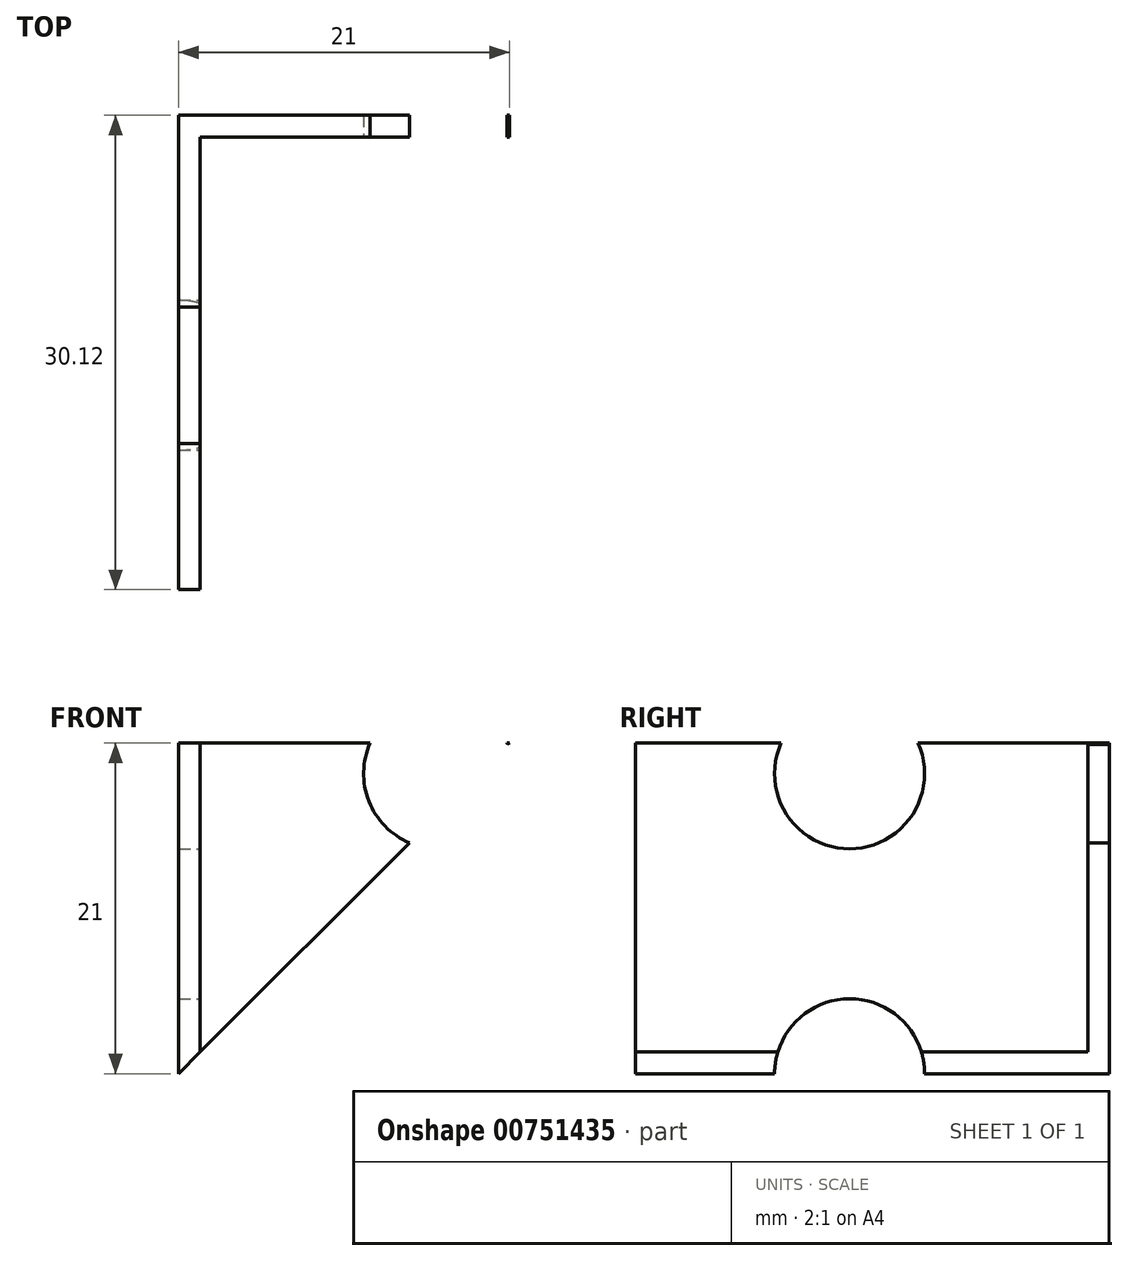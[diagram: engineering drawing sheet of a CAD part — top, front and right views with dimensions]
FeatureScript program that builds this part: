
annotation { "Feature Type Name" : "Feature", "Feature Type Description" : "" }
export const myFeature = defineFeature(function(context is Context, id is Id, definition is map)
    precondition{}
    {
        {
            assignVariable(context, id + "F0", {"name" : "height", "anyValue" : 21});
        }
        {
            var Q0;
            Q0=qCreatedBy(makeId("Top.planeOp"),FACE);
            var sketch = newSketch(context, id + "F1", { "sketchPlane" : qUnion([Q0])});
            skLineSegment(sketch, "E0", {"start": v(-1.37, -28.75) * mm, "end": v(-1.37, 1.37) * mm});
            skLineSegment(sketch, "E1", {"start": v(-1.37, 1.37) * mm, "end": v(28.75, 1.37) * mm});
            skLineSegment(sketch, "E2", {"start": v(28.75, 1.37) * mm, "end": v(28.75, 0) * mm});
            skLineSegment(sketch, "E3", {"start": v(28.75, 0) * mm, "end": v(0, 0) * mm});
            skLineSegment(sketch, "E4", {"start": v(0, 0) * mm, "end": v(0, -28.75) * mm});
            skLineSegment(sketch, "E5", {"start": v(0, -28.75) * mm, "end": v(-1.37, -28.75) * mm});
            skSolve(sketch);
        }
        {
            var Q0;
            Q0=makeQuery(id+"F1.imprint","IMPRINT",FACE,{"disambiguationData":[TD([[makeQuery(id+"F1.imprint","IMPRINT",EDGE,{"derivedFrom":sQuery(id+"F1.wireOp",EDGE,"E0")}),-1.0]])]});
            extrude(context, id + "F2", {"entities" : qUnion([Q0]), "depth" : (getVariable(context, 'height')) * mm, "offsetDistance" : 25.4 * mm});
        }
        {
            var Q0;
            Q0=makeQuery(id+"F2.opExtrude","SWEPT_FACE",FACE,{"disambiguationData":[OSD([sQuery(id+"F1.wireOp",EDGE,"E3")])]});
            var sketch = newSketch(context, id + "F3", { "sketchPlane" : qUnion([Q0])});
            skPoint(sketch, "E6", {"position": v(15.14, 19.05) * mm});
            skLineSegment(sketch, "E7", {"start": v(15.14, 0) * mm, "end": v(15.14, 533.4) * mm, "construction": true});
            skCircle(sketch, "E8", {"center": v(15.14, 19.05) * mm, "radius": 4.76 * mm});
            skCircle(sketch, "E9", {"center": v(15.14, 0) * mm, "radius": 4.76 * mm});
            skPoint(sketch, "E10", {"position": v(15.14, 38.1) * mm});
            skPoint(sketch, "E11", {"position": v(15.14, 57.15) * mm});
            skArc(sketch, "E12", {"start": v(19.9, 39.69) * mm, "mid": v(15.14, 44.45) * mm, "end": v(10.38, 39.69) * mm});
            skArc(sketch, "E13", {"start": v(10.38, 36.51) * mm, "mid": v(15.14, 31.75) * mm, "end": v(19.9, 36.51) * mm});
            skLineSegment(sketch, "E14", {"start": v(19.9, 39.69) * mm, "end": v(19.9, 36.51) * mm});
            skLineSegment(sketch, "E15", {"start": v(10.38, 39.69) * mm, "end": v(10.38, 36.51) * mm});
            skArc(sketch, "E16", {"start": v(19.9, 58.74) * mm, "mid": v(15.14, 63.5) * mm, "end": v(10.38, 58.74) * mm});
            skArc(sketch, "E17", {"start": v(10.38, 55.56) * mm, "mid": v(15.14, 50.8) * mm, "end": v(19.9, 55.56) * mm});
            skLineSegment(sketch, "E18", {"start": v(19.9, 58.74) * mm, "end": v(19.9, 55.56) * mm});
            skLineSegment(sketch, "E19", {"start": v(10.38, 58.74) * mm, "end": v(10.38, 55.56) * mm});
            skPoint(sketch, "E20.0.1.0", {"position": v(15.14, 133.35) * mm});
            skArc(sketch, "E20.0.1.1", {"start": v(19.9, 134.94) * mm, "mid": v(15.14, 139.7) * mm, "end": v(10.38, 134.94) * mm});
            skPoint(sketch, "E20.0.1.2", {"position": v(15.14, 114.3) * mm});
            skPoint(sketch, "E20.0.1.3", {"position": v(15.14, 95.25) * mm});
            skArc(sketch, "E20.0.1.4", {"start": v(10.38, 131.76) * mm, "mid": v(15.14, 127) * mm, "end": v(19.9, 131.76) * mm});
            skCircle(sketch, "E20.0.1.5", {"center": v(15.14, 95.25) * mm, "radius": 4.76 * mm});
            skCircle(sketch, "E20.0.1.6", {"center": v(15.14, 76.2) * mm, "radius": 4.76 * mm});
            skArc(sketch, "E20.0.1.7", {"start": v(19.9, 115.89) * mm, "mid": v(15.14, 120.65) * mm, "end": v(10.38, 115.89) * mm});
            skArc(sketch, "E20.0.1.8", {"start": v(10.38, 112.71) * mm, "mid": v(15.14, 107.95) * mm, "end": v(19.9, 112.71) * mm});
            skPoint(sketch, "E20.0.1.9", {"position": v(15.14, 133.35) * mm});
            skPoint(sketch, "E20.0.1.10", {"position": v(15.14, 114.3) * mm});
            skLineSegment(sketch, "E20.0.1.11", {"start": v(10.38, 134.94) * mm, "end": v(10.38, 131.76) * mm});
            skLineSegment(sketch, "E20.0.1.12", {"start": v(19.9, 134.94) * mm, "end": v(19.9, 131.76) * mm});
            skLineSegment(sketch, "E20.0.1.13", {"start": v(19.9, 115.89) * mm, "end": v(19.9, 112.71) * mm});
            skLineSegment(sketch, "E20.0.1.14", {"start": v(10.38, 115.89) * mm, "end": v(10.38, 112.71) * mm});
            skPoint(sketch, "E20.0.2.0", {"position": v(15.14, 209.55) * mm});
            skArc(sketch, "E20.0.2.1", {"start": v(19.9, 211.14) * mm, "mid": v(15.14, 215.9) * mm, "end": v(10.38, 211.14) * mm});
            skPoint(sketch, "E20.0.2.2", {"position": v(15.14, 190.5) * mm});
            skPoint(sketch, "E20.0.2.3", {"position": v(15.14, 171.45) * mm});
            skArc(sketch, "E20.0.2.4", {"start": v(10.38, 207.96) * mm, "mid": v(15.14, 203.2) * mm, "end": v(19.9, 207.96) * mm});
            skCircle(sketch, "E20.0.2.5", {"center": v(15.14, 171.45) * mm, "radius": 4.76 * mm});
            skCircle(sketch, "E20.0.2.6", {"center": v(15.14, 152.4) * mm, "radius": 4.76 * mm});
            skArc(sketch, "E20.0.2.7", {"start": v(19.9, 192.09) * mm, "mid": v(15.14, 196.85) * mm, "end": v(10.38, 192.09) * mm});
            skArc(sketch, "E20.0.2.8", {"start": v(10.38, 188.91) * mm, "mid": v(15.14, 184.15) * mm, "end": v(19.9, 188.91) * mm});
            skPoint(sketch, "E20.0.2.9", {"position": v(15.14, 209.55) * mm});
            skPoint(sketch, "E20.0.2.10", {"position": v(15.14, 190.5) * mm});
            skLineSegment(sketch, "E20.0.2.11", {"start": v(10.38, 211.14) * mm, "end": v(10.38, 207.96) * mm});
            skLineSegment(sketch, "E20.0.2.12", {"start": v(19.9, 211.14) * mm, "end": v(19.9, 207.96) * mm});
            skLineSegment(sketch, "E20.0.2.13", {"start": v(19.9, 192.09) * mm, "end": v(19.9, 188.91) * mm});
            skLineSegment(sketch, "E20.0.2.14", {"start": v(10.38, 192.09) * mm, "end": v(10.38, 188.91) * mm});
            skPoint(sketch, "E20.0.3.0", {"position": v(15.14, 285.75) * mm});
            skArc(sketch, "E20.0.3.1", {"start": v(19.9, 287.34) * mm, "mid": v(15.14, 292.1) * mm, "end": v(10.38, 287.34) * mm});
            skPoint(sketch, "E20.0.3.2", {"position": v(15.14, 266.7) * mm});
            skPoint(sketch, "E20.0.3.3", {"position": v(15.14, 247.65) * mm});
            skArc(sketch, "E20.0.3.4", {"start": v(10.38, 284.16) * mm, "mid": v(15.14, 279.4) * mm, "end": v(19.9, 284.16) * mm});
            skCircle(sketch, "E20.0.3.5", {"center": v(15.14, 247.65) * mm, "radius": 4.76 * mm});
            skCircle(sketch, "E20.0.3.6", {"center": v(15.14, 228.6) * mm, "radius": 4.76 * mm});
            skArc(sketch, "E20.0.3.7", {"start": v(19.9, 268.29) * mm, "mid": v(15.14, 273.05) * mm, "end": v(10.38, 268.29) * mm});
            skArc(sketch, "E20.0.3.8", {"start": v(10.38, 265.11) * mm, "mid": v(15.14, 260.35) * mm, "end": v(19.9, 265.11) * mm});
            skPoint(sketch, "E20.0.3.9", {"position": v(15.14, 285.75) * mm});
            skPoint(sketch, "E20.0.3.10", {"position": v(15.14, 266.7) * mm});
            skLineSegment(sketch, "E20.0.3.11", {"start": v(10.38, 287.34) * mm, "end": v(10.38, 284.16) * mm});
            skLineSegment(sketch, "E20.0.3.12", {"start": v(19.9, 287.34) * mm, "end": v(19.9, 284.16) * mm});
            skLineSegment(sketch, "E20.0.3.13", {"start": v(19.9, 268.29) * mm, "end": v(19.9, 265.11) * mm});
            skLineSegment(sketch, "E20.0.3.14", {"start": v(10.38, 268.29) * mm, "end": v(10.38, 265.11) * mm});
            skPoint(sketch, "E20.0.4.0", {"position": v(15.14, 361.95) * mm});
            skArc(sketch, "E20.0.4.1", {"start": v(19.9, 363.54) * mm, "mid": v(15.14, 368.3) * mm, "end": v(10.38, 363.54) * mm});
            skPoint(sketch, "E20.0.4.2", {"position": v(15.14, 342.9) * mm});
            skPoint(sketch, "E20.0.4.3", {"position": v(15.14, 323.85) * mm});
            skArc(sketch, "E20.0.4.4", {"start": v(10.38, 360.36) * mm, "mid": v(15.14, 355.6) * mm, "end": v(19.9, 360.36) * mm});
            skCircle(sketch, "E20.0.4.5", {"center": v(15.14, 323.85) * mm, "radius": 4.76 * mm});
            skCircle(sketch, "E20.0.4.6", {"center": v(15.14, 304.8) * mm, "radius": 4.76 * mm});
            skArc(sketch, "E20.0.4.7", {"start": v(19.9, 344.49) * mm, "mid": v(15.14, 349.25) * mm, "end": v(10.38, 344.49) * mm});
            skArc(sketch, "E20.0.4.8", {"start": v(10.38, 341.31) * mm, "mid": v(15.14, 336.55) * mm, "end": v(19.9, 341.31) * mm});
            skPoint(sketch, "E20.0.4.9", {"position": v(15.14, 361.95) * mm});
            skPoint(sketch, "E20.0.4.10", {"position": v(15.14, 342.9) * mm});
            skLineSegment(sketch, "E20.0.4.11", {"start": v(10.38, 363.54) * mm, "end": v(10.38, 360.36) * mm});
            skLineSegment(sketch, "E20.0.4.12", {"start": v(19.9, 363.54) * mm, "end": v(19.9, 360.36) * mm});
            skLineSegment(sketch, "E20.0.4.13", {"start": v(19.9, 344.49) * mm, "end": v(19.9, 341.31) * mm});
            skLineSegment(sketch, "E20.0.4.14", {"start": v(10.38, 344.49) * mm, "end": v(10.38, 341.31) * mm});
            skPoint(sketch, "E20.0.5.0", {"position": v(15.14, 438.15) * mm});
            skArc(sketch, "E20.0.5.1", {"start": v(19.9, 439.74) * mm, "mid": v(15.14, 444.5) * mm, "end": v(10.38, 439.74) * mm});
            skPoint(sketch, "E20.0.5.2", {"position": v(15.14, 419.1) * mm});
            skPoint(sketch, "E20.0.5.3", {"position": v(15.14, 400.05) * mm});
            skArc(sketch, "E20.0.5.4", {"start": v(10.38, 436.56) * mm, "mid": v(15.14, 431.8) * mm, "end": v(19.9, 436.56) * mm});
            skCircle(sketch, "E20.0.5.5", {"center": v(15.14, 400.05) * mm, "radius": 4.76 * mm});
            skCircle(sketch, "E20.0.5.6", {"center": v(15.14, 381) * mm, "radius": 4.76 * mm});
            skArc(sketch, "E20.0.5.7", {"start": v(19.9, 420.69) * mm, "mid": v(15.14, 425.45) * mm, "end": v(10.38, 420.69) * mm});
            skArc(sketch, "E20.0.5.8", {"start": v(10.38, 417.51) * mm, "mid": v(15.14, 412.75) * mm, "end": v(19.9, 417.51) * mm});
            skPoint(sketch, "E20.0.5.9", {"position": v(15.14, 438.15) * mm});
            skPoint(sketch, "E20.0.5.10", {"position": v(15.14, 419.1) * mm});
            skLineSegment(sketch, "E20.0.5.11", {"start": v(10.38, 439.74) * mm, "end": v(10.38, 436.56) * mm});
            skLineSegment(sketch, "E20.0.5.12", {"start": v(19.9, 439.74) * mm, "end": v(19.9, 436.56) * mm});
            skLineSegment(sketch, "E20.0.5.13", {"start": v(19.9, 420.69) * mm, "end": v(19.9, 417.51) * mm});
            skLineSegment(sketch, "E20.0.5.14", {"start": v(10.38, 420.69) * mm, "end": v(10.38, 417.51) * mm});
            skPoint(sketch, "E20.0.6.0", {"position": v(15.14, 514.35) * mm});
            skArc(sketch, "E20.0.6.1", {"start": v(19.9, 515.94) * mm, "mid": v(15.14, 520.7) * mm, "end": v(10.38, 515.94) * mm});
            skPoint(sketch, "E20.0.6.2", {"position": v(15.14, 495.3) * mm});
            skPoint(sketch, "E20.0.6.3", {"position": v(15.14, 476.25) * mm});
            skArc(sketch, "E20.0.6.4", {"start": v(10.38, 512.76) * mm, "mid": v(15.14, 508) * mm, "end": v(19.9, 512.76) * mm});
            skCircle(sketch, "E20.0.6.5", {"center": v(15.14, 476.25) * mm, "radius": 4.76 * mm});
            skCircle(sketch, "E20.0.6.6", {"center": v(15.14, 457.2) * mm, "radius": 4.76 * mm});
            skArc(sketch, "E20.0.6.7", {"start": v(19.9, 496.89) * mm, "mid": v(15.14, 501.65) * mm, "end": v(10.38, 496.89) * mm});
            skArc(sketch, "E20.0.6.8", {"start": v(10.38, 493.71) * mm, "mid": v(15.14, 488.95) * mm, "end": v(19.9, 493.71) * mm});
            skPoint(sketch, "E20.0.6.9", {"position": v(15.14, 514.35) * mm});
            skPoint(sketch, "E20.0.6.10", {"position": v(15.14, 495.3) * mm});
            skLineSegment(sketch, "E20.0.6.11", {"start": v(10.38, 515.94) * mm, "end": v(10.38, 512.76) * mm});
            skLineSegment(sketch, "E20.0.6.12", {"start": v(19.9, 515.94) * mm, "end": v(19.9, 512.76) * mm});
            skLineSegment(sketch, "E20.0.6.13", {"start": v(19.9, 496.89) * mm, "end": v(19.9, 493.71) * mm});
            skLineSegment(sketch, "E20.0.6.14", {"start": v(10.38, 496.89) * mm, "end": v(10.38, 493.71) * mm});
            skPoint(sketch, "E20.0.7.0", {"position": v(15.14, 590.55) * mm});
            skArc(sketch, "E20.0.7.1", {"start": v(19.9, 592.14) * mm, "mid": v(15.14, 596.9) * mm, "end": v(10.38, 592.14) * mm});
            skPoint(sketch, "E20.0.7.2", {"position": v(15.14, 571.5) * mm});
            skPoint(sketch, "E20.0.7.3", {"position": v(15.14, 552.45) * mm});
            skArc(sketch, "E20.0.7.4", {"start": v(10.38, 588.96) * mm, "mid": v(15.14, 584.2) * mm, "end": v(19.9, 588.96) * mm});
            skCircle(sketch, "E20.0.7.5", {"center": v(15.14, 552.45) * mm, "radius": 4.76 * mm});
            skCircle(sketch, "E20.0.7.6", {"center": v(15.14, 533.4) * mm, "radius": 4.76 * mm});
            skArc(sketch, "E20.0.7.7", {"start": v(19.9, 573.09) * mm, "mid": v(15.14, 577.85) * mm, "end": v(10.38, 573.09) * mm});
            skArc(sketch, "E20.0.7.8", {"start": v(10.38, 569.91) * mm, "mid": v(15.14, 565.15) * mm, "end": v(19.9, 569.91) * mm});
            skPoint(sketch, "E20.0.7.9", {"position": v(15.14, 590.55) * mm});
            skPoint(sketch, "E20.0.7.10", {"position": v(15.14, 571.5) * mm});
            skLineSegment(sketch, "E20.0.7.11", {"start": v(10.38, 592.14) * mm, "end": v(10.38, 588.96) * mm});
            skLineSegment(sketch, "E20.0.7.12", {"start": v(19.9, 592.14) * mm, "end": v(19.9, 588.96) * mm});
            skLineSegment(sketch, "E20.0.7.13", {"start": v(19.9, 573.09) * mm, "end": v(19.9, 569.91) * mm});
            skLineSegment(sketch, "E20.0.7.14", {"start": v(10.38, 573.09) * mm, "end": v(10.38, 569.91) * mm});
            skPoint(sketch, "E20.0.8.0", {"position": v(15.14, 666.75) * mm});
            skArc(sketch, "E20.0.8.1", {"start": v(19.9, 668.34) * mm, "mid": v(15.14, 673.1) * mm, "end": v(10.38, 668.34) * mm});
            skPoint(sketch, "E20.0.8.2", {"position": v(15.14, 647.7) * mm});
            skPoint(sketch, "E20.0.8.3", {"position": v(15.14, 628.65) * mm});
            skArc(sketch, "E20.0.8.4", {"start": v(10.38, 665.16) * mm, "mid": v(15.14, 660.4) * mm, "end": v(19.9, 665.16) * mm});
            skCircle(sketch, "E20.0.8.5", {"center": v(15.14, 628.65) * mm, "radius": 4.76 * mm});
            skCircle(sketch, "E20.0.8.6", {"center": v(15.14, 609.6) * mm, "radius": 4.76 * mm});
            skArc(sketch, "E20.0.8.7", {"start": v(19.9, 649.29) * mm, "mid": v(15.14, 654.05) * mm, "end": v(10.38, 649.29) * mm});
            skArc(sketch, "E20.0.8.8", {"start": v(10.38, 646.11) * mm, "mid": v(15.14, 641.35) * mm, "end": v(19.9, 646.11) * mm});
            skPoint(sketch, "E20.0.8.9", {"position": v(15.14, 666.75) * mm});
            skPoint(sketch, "E20.0.8.10", {"position": v(15.14, 647.7) * mm});
            skLineSegment(sketch, "E20.0.8.11", {"start": v(10.38, 668.34) * mm, "end": v(10.38, 665.16) * mm});
            skLineSegment(sketch, "E20.0.8.12", {"start": v(19.9, 668.34) * mm, "end": v(19.9, 665.16) * mm});
            skLineSegment(sketch, "E20.0.8.13", {"start": v(19.9, 649.29) * mm, "end": v(19.9, 646.11) * mm});
            skLineSegment(sketch, "E20.0.8.14", {"start": v(10.38, 649.29) * mm, "end": v(10.38, 646.11) * mm});
            skPoint(sketch, "E20.0.9.0", {"position": v(15.14, 742.95) * mm});
            skArc(sketch, "E20.0.9.1", {"start": v(19.9, 744.54) * mm, "mid": v(15.14, 749.3) * mm, "end": v(10.38, 744.54) * mm});
            skPoint(sketch, "E20.0.9.2", {"position": v(15.14, 723.9) * mm});
            skPoint(sketch, "E20.0.9.3", {"position": v(15.14, 704.85) * mm});
            skArc(sketch, "E20.0.9.4", {"start": v(10.38, 741.36) * mm, "mid": v(15.14, 736.6) * mm, "end": v(19.9, 741.36) * mm});
            skCircle(sketch, "E20.0.9.5", {"center": v(15.14, 704.85) * mm, "radius": 4.76 * mm});
            skCircle(sketch, "E20.0.9.6", {"center": v(15.14, 685.8) * mm, "radius": 4.76 * mm});
            skArc(sketch, "E20.0.9.7", {"start": v(19.9, 725.49) * mm, "mid": v(15.14, 730.25) * mm, "end": v(10.38, 725.49) * mm});
            skArc(sketch, "E20.0.9.8", {"start": v(10.38, 722.31) * mm, "mid": v(15.14, 717.55) * mm, "end": v(19.9, 722.31) * mm});
            skPoint(sketch, "E20.0.9.9", {"position": v(15.14, 742.95) * mm});
            skPoint(sketch, "E20.0.9.10", {"position": v(15.14, 723.9) * mm});
            skLineSegment(sketch, "E20.0.9.11", {"start": v(10.38, 744.54) * mm, "end": v(10.38, 741.36) * mm});
            skLineSegment(sketch, "E20.0.9.12", {"start": v(19.9, 744.54) * mm, "end": v(19.9, 741.36) * mm});
            skLineSegment(sketch, "E20.0.9.13", {"start": v(19.9, 725.49) * mm, "end": v(19.9, 722.31) * mm});
            skLineSegment(sketch, "E20.0.9.14", {"start": v(10.38, 725.49) * mm, "end": v(10.38, 722.31) * mm});
            skPoint(sketch, "E20.0.10.0", {"position": v(15.14, 819.15) * mm});
            skArc(sketch, "E20.0.10.1", {"start": v(19.9, 820.74) * mm, "mid": v(15.14, 825.5) * mm, "end": v(10.38, 820.74) * mm});
            skPoint(sketch, "E20.0.10.2", {"position": v(15.14, 800.1) * mm});
            skPoint(sketch, "E20.0.10.3", {"position": v(15.14, 781.05) * mm});
            skArc(sketch, "E20.0.10.4", {"start": v(10.38, 817.56) * mm, "mid": v(15.14, 812.8) * mm, "end": v(19.9, 817.56) * mm});
            skCircle(sketch, "E20.0.10.5", {"center": v(15.14, 781.05) * mm, "radius": 4.76 * mm});
            skCircle(sketch, "E20.0.10.6", {"center": v(15.14, 762) * mm, "radius": 4.76 * mm});
            skArc(sketch, "E20.0.10.7", {"start": v(19.9, 801.69) * mm, "mid": v(15.14, 806.45) * mm, "end": v(10.38, 801.69) * mm});
            skArc(sketch, "E20.0.10.8", {"start": v(10.38, 798.51) * mm, "mid": v(15.14, 793.75) * mm, "end": v(19.9, 798.51) * mm});
            skPoint(sketch, "E20.0.10.9", {"position": v(15.14, 819.15) * mm});
            skPoint(sketch, "E20.0.10.10", {"position": v(15.14, 800.1) * mm});
            skLineSegment(sketch, "E20.0.10.11", {"start": v(10.38, 820.74) * mm, "end": v(10.38, 817.56) * mm});
            skLineSegment(sketch, "E20.0.10.12", {"start": v(19.9, 820.74) * mm, "end": v(19.9, 817.56) * mm});
            skLineSegment(sketch, "E20.0.10.13", {"start": v(19.9, 801.69) * mm, "end": v(19.9, 798.51) * mm});
            skLineSegment(sketch, "E20.0.10.14", {"start": v(10.38, 801.69) * mm, "end": v(10.38, 798.51) * mm});
            skPoint(sketch, "E20.0.11.0", {"position": v(15.14, 895.35) * mm});
            skArc(sketch, "E20.0.11.1", {"start": v(19.9, 896.94) * mm, "mid": v(15.14, 901.7) * mm, "end": v(10.38, 896.94) * mm});
            skPoint(sketch, "E20.0.11.2", {"position": v(15.14, 876.3) * mm});
            skPoint(sketch, "E20.0.11.3", {"position": v(15.14, 857.25) * mm});
            skArc(sketch, "E20.0.11.4", {"start": v(10.38, 893.76) * mm, "mid": v(15.14, 889) * mm, "end": v(19.9, 893.76) * mm});
            skCircle(sketch, "E20.0.11.5", {"center": v(15.14, 857.25) * mm, "radius": 4.76 * mm});
            skCircle(sketch, "E20.0.11.6", {"center": v(15.14, 838.2) * mm, "radius": 4.76 * mm});
            skArc(sketch, "E20.0.11.7", {"start": v(19.9, 877.89) * mm, "mid": v(15.14, 882.65) * mm, "end": v(10.38, 877.89) * mm});
            skArc(sketch, "E20.0.11.8", {"start": v(10.38, 874.71) * mm, "mid": v(15.14, 869.95) * mm, "end": v(19.9, 874.71) * mm});
            skPoint(sketch, "E20.0.11.9", {"position": v(15.14, 895.35) * mm});
            skPoint(sketch, "E20.0.11.10", {"position": v(15.14, 876.3) * mm});
            skLineSegment(sketch, "E20.0.11.11", {"start": v(10.38, 896.94) * mm, "end": v(10.38, 893.76) * mm});
            skLineSegment(sketch, "E20.0.11.12", {"start": v(19.9, 896.94) * mm, "end": v(19.9, 893.76) * mm});
            skLineSegment(sketch, "E20.0.11.13", {"start": v(19.9, 877.89) * mm, "end": v(19.9, 874.71) * mm});
            skLineSegment(sketch, "E20.0.11.14", {"start": v(10.38, 877.89) * mm, "end": v(10.38, 874.71) * mm});
            skPoint(sketch, "E20.0.12.0", {"position": v(15.14, 971.55) * mm});
            skArc(sketch, "E20.0.12.1", {"start": v(19.9, 973.14) * mm, "mid": v(15.14, 977.9) * mm, "end": v(10.38, 973.14) * mm});
            skPoint(sketch, "E20.0.12.2", {"position": v(15.14, 952.5) * mm});
            skPoint(sketch, "E20.0.12.3", {"position": v(15.14, 933.45) * mm});
            skArc(sketch, "E20.0.12.4", {"start": v(10.38, 969.96) * mm, "mid": v(15.14, 965.2) * mm, "end": v(19.9, 969.96) * mm});
            skCircle(sketch, "E20.0.12.5", {"center": v(15.14, 933.45) * mm, "radius": 4.76 * mm});
            skCircle(sketch, "E20.0.12.6", {"center": v(15.14, 914.4) * mm, "radius": 4.76 * mm});
            skArc(sketch, "E20.0.12.7", {"start": v(19.9, 954.09) * mm, "mid": v(15.14, 958.85) * mm, "end": v(10.38, 954.09) * mm});
            skArc(sketch, "E20.0.12.8", {"start": v(10.38, 950.91) * mm, "mid": v(15.14, 946.15) * mm, "end": v(19.9, 950.91) * mm});
            skPoint(sketch, "E20.0.12.9", {"position": v(15.14, 971.55) * mm});
            skPoint(sketch, "E20.0.12.10", {"position": v(15.14, 952.5) * mm});
            skLineSegment(sketch, "E20.0.12.11", {"start": v(10.38, 973.14) * mm, "end": v(10.38, 969.96) * mm});
            skLineSegment(sketch, "E20.0.12.12", {"start": v(19.9, 973.14) * mm, "end": v(19.9, 969.96) * mm});
            skLineSegment(sketch, "E20.0.12.13", {"start": v(19.9, 954.09) * mm, "end": v(19.9, 950.91) * mm});
            skLineSegment(sketch, "E20.0.12.14", {"start": v(10.38, 954.09) * mm, "end": v(10.38, 950.91) * mm});
            skPoint(sketch, "E20.0.13.0", {"position": v(15.14, 1047.75) * mm});
            skArc(sketch, "E20.0.13.1", {"start": v(19.9, 1049.34) * mm, "mid": v(15.14, 1054.1) * mm, "end": v(10.38, 1049.34) * mm});
            skPoint(sketch, "E20.0.13.2", {"position": v(15.14, 1028.7) * mm});
            skPoint(sketch, "E20.0.13.3", {"position": v(15.14, 1009.65) * mm});
            skArc(sketch, "E20.0.13.4", {"start": v(10.38, 1046.16) * mm, "mid": v(15.14, 1041.4) * mm, "end": v(19.9, 1046.16) * mm});
            skCircle(sketch, "E20.0.13.5", {"center": v(15.14, 1009.65) * mm, "radius": 4.76 * mm});
            skCircle(sketch, "E20.0.13.6", {"center": v(15.14, 990.6) * mm, "radius": 4.76 * mm});
            skArc(sketch, "E20.0.13.7", {"start": v(19.9, 1030.29) * mm, "mid": v(15.14, 1035.05) * mm, "end": v(10.38, 1030.29) * mm});
            skArc(sketch, "E20.0.13.8", {"start": v(10.38, 1027.11) * mm, "mid": v(15.14, 1022.35) * mm, "end": v(19.9, 1027.11) * mm});
            skPoint(sketch, "E20.0.13.9", {"position": v(15.14, 1047.75) * mm});
            skPoint(sketch, "E20.0.13.10", {"position": v(15.14, 1028.7) * mm});
            skLineSegment(sketch, "E20.0.13.11", {"start": v(10.38, 1049.34) * mm, "end": v(10.38, 1046.16) * mm});
            skLineSegment(sketch, "E20.0.13.12", {"start": v(19.9, 1049.34) * mm, "end": v(19.9, 1046.16) * mm});
            skLineSegment(sketch, "E20.0.13.13", {"start": v(19.9, 1030.29) * mm, "end": v(19.9, 1027.11) * mm});
            skLineSegment(sketch, "E20.0.13.14", {"start": v(10.38, 1030.29) * mm, "end": v(10.38, 1027.11) * mm});
            skPoint(sketch, "E20.0.14.0", {"position": v(15.14, 1123.95) * mm});
            skArc(sketch, "E20.0.14.1", {"start": v(19.9, 1125.54) * mm, "mid": v(15.14, 1130.3) * mm, "end": v(10.38, 1125.54) * mm});
            skPoint(sketch, "E20.0.14.2", {"position": v(15.14, 1104.9) * mm});
            skPoint(sketch, "E20.0.14.3", {"position": v(15.14, 1085.85) * mm});
            skArc(sketch, "E20.0.14.4", {"start": v(10.38, 1122.36) * mm, "mid": v(15.14, 1117.6) * mm, "end": v(19.9, 1122.36) * mm});
            skCircle(sketch, "E20.0.14.5", {"center": v(15.14, 1085.85) * mm, "radius": 4.76 * mm});
            skCircle(sketch, "E20.0.14.6", {"center": v(15.14, 1066.8) * mm, "radius": 4.76 * mm});
            skArc(sketch, "E20.0.14.7", {"start": v(19.9, 1106.49) * mm, "mid": v(15.14, 1111.25) * mm, "end": v(10.38, 1106.49) * mm});
            skArc(sketch, "E20.0.14.8", {"start": v(10.38, 1103.31) * mm, "mid": v(15.14, 1098.55) * mm, "end": v(19.9, 1103.31) * mm});
            skPoint(sketch, "E20.0.14.9", {"position": v(15.14, 1123.95) * mm});
            skPoint(sketch, "E20.0.14.10", {"position": v(15.14, 1104.9) * mm});
            skLineSegment(sketch, "E20.0.14.11", {"start": v(10.38, 1125.54) * mm, "end": v(10.38, 1122.36) * mm});
            skLineSegment(sketch, "E20.0.14.12", {"start": v(19.9, 1125.54) * mm, "end": v(19.9, 1122.36) * mm});
            skLineSegment(sketch, "E20.0.14.13", {"start": v(19.9, 1106.49) * mm, "end": v(19.9, 1103.31) * mm});
            skLineSegment(sketch, "E20.0.14.14", {"start": v(10.38, 1106.49) * mm, "end": v(10.38, 1103.31) * mm});
            skPoint(sketch, "E20.0.15.0", {"position": v(15.14, 1200.15) * mm});
            skArc(sketch, "E20.0.15.1", {"start": v(19.9, 1201.74) * mm, "mid": v(15.14, 1206.5) * mm, "end": v(10.38, 1201.74) * mm});
            skPoint(sketch, "E20.0.15.2", {"position": v(15.14, 1181.1) * mm});
            skPoint(sketch, "E20.0.15.3", {"position": v(15.14, 1162.05) * mm});
            skArc(sketch, "E20.0.15.4", {"start": v(10.38, 1198.56) * mm, "mid": v(15.14, 1193.8) * mm, "end": v(19.9, 1198.56) * mm});
            skCircle(sketch, "E20.0.15.5", {"center": v(15.14, 1162.05) * mm, "radius": 4.76 * mm});
            skCircle(sketch, "E20.0.15.6", {"center": v(15.14, 1143) * mm, "radius": 4.76 * mm});
            skArc(sketch, "E20.0.15.7", {"start": v(19.9, 1182.69) * mm, "mid": v(15.14, 1187.45) * mm, "end": v(10.38, 1182.69) * mm});
            skArc(sketch, "E20.0.15.8", {"start": v(10.38, 1179.51) * mm, "mid": v(15.14, 1174.75) * mm, "end": v(19.9, 1179.51) * mm});
            skPoint(sketch, "E20.0.15.9", {"position": v(15.14, 1200.15) * mm});
            skPoint(sketch, "E20.0.15.10", {"position": v(15.14, 1181.1) * mm});
            skLineSegment(sketch, "E20.0.15.11", {"start": v(10.38, 1201.74) * mm, "end": v(10.38, 1198.56) * mm});
            skLineSegment(sketch, "E20.0.15.12", {"start": v(19.9, 1201.74) * mm, "end": v(19.9, 1198.56) * mm});
            skLineSegment(sketch, "E20.0.15.13", {"start": v(19.9, 1182.69) * mm, "end": v(19.9, 1179.51) * mm});
            skLineSegment(sketch, "E20.0.15.14", {"start": v(10.38, 1182.69) * mm, "end": v(10.38, 1179.51) * mm});
            skPoint(sketch, "E20.0.16.0", {"position": v(15.14, 1276.35) * mm});
            skArc(sketch, "E20.0.16.1", {"start": v(19.9, 1277.94) * mm, "mid": v(15.14, 1282.7) * mm, "end": v(10.38, 1277.94) * mm});
            skPoint(sketch, "E20.0.16.2", {"position": v(15.14, 1257.3) * mm});
            skPoint(sketch, "E20.0.16.3", {"position": v(15.14, 1238.25) * mm});
            skArc(sketch, "E20.0.16.4", {"start": v(10.38, 1274.76) * mm, "mid": v(15.14, 1270) * mm, "end": v(19.9, 1274.76) * mm});
            skCircle(sketch, "E20.0.16.5", {"center": v(15.14, 1238.25) * mm, "radius": 4.76 * mm});
            skCircle(sketch, "E20.0.16.6", {"center": v(15.14, 1219.2) * mm, "radius": 4.76 * mm});
            skArc(sketch, "E20.0.16.7", {"start": v(19.9, 1258.89) * mm, "mid": v(15.14, 1263.65) * mm, "end": v(10.38, 1258.89) * mm});
            skArc(sketch, "E20.0.16.8", {"start": v(10.38, 1255.71) * mm, "mid": v(15.14, 1250.95) * mm, "end": v(19.9, 1255.71) * mm});
            skPoint(sketch, "E20.0.16.9", {"position": v(15.14, 1276.35) * mm});
            skPoint(sketch, "E20.0.16.10", {"position": v(15.14, 1257.3) * mm});
            skLineSegment(sketch, "E20.0.16.11", {"start": v(10.38, 1277.94) * mm, "end": v(10.38, 1274.76) * mm});
            skLineSegment(sketch, "E20.0.16.12", {"start": v(19.9, 1277.94) * mm, "end": v(19.9, 1274.76) * mm});
            skLineSegment(sketch, "E20.0.16.13", {"start": v(19.9, 1258.89) * mm, "end": v(19.9, 1255.71) * mm});
            skLineSegment(sketch, "E20.0.16.14", {"start": v(10.38, 1258.89) * mm, "end": v(10.38, 1255.71) * mm});
            skPoint(sketch, "E20.0.17.0", {"position": v(15.14, 1352.55) * mm});
            skArc(sketch, "E20.0.17.1", {"start": v(19.9, 1354.14) * mm, "mid": v(15.14, 1358.9) * mm, "end": v(10.38, 1354.14) * mm});
            skPoint(sketch, "E20.0.17.2", {"position": v(15.14, 1333.5) * mm});
            skPoint(sketch, "E20.0.17.3", {"position": v(15.14, 1314.45) * mm});
            skArc(sketch, "E20.0.17.4", {"start": v(10.38, 1350.96) * mm, "mid": v(15.14, 1346.2) * mm, "end": v(19.9, 1350.96) * mm});
            skCircle(sketch, "E20.0.17.5", {"center": v(15.14, 1314.45) * mm, "radius": 4.76 * mm});
            skCircle(sketch, "E20.0.17.6", {"center": v(15.14, 1295.4) * mm, "radius": 4.76 * mm});
            skArc(sketch, "E20.0.17.7", {"start": v(19.9, 1335.09) * mm, "mid": v(15.14, 1339.85) * mm, "end": v(10.38, 1335.09) * mm});
            skArc(sketch, "E20.0.17.8", {"start": v(10.38, 1331.91) * mm, "mid": v(15.14, 1327.15) * mm, "end": v(19.9, 1331.91) * mm});
            skPoint(sketch, "E20.0.17.9", {"position": v(15.14, 1352.55) * mm});
            skPoint(sketch, "E20.0.17.10", {"position": v(15.14, 1333.5) * mm});
            skLineSegment(sketch, "E20.0.17.11", {"start": v(10.38, 1354.14) * mm, "end": v(10.38, 1350.96) * mm});
            skLineSegment(sketch, "E20.0.17.12", {"start": v(19.9, 1354.14) * mm, "end": v(19.9, 1350.96) * mm});
            skLineSegment(sketch, "E20.0.17.13", {"start": v(19.9, 1335.09) * mm, "end": v(19.9, 1331.91) * mm});
            skLineSegment(sketch, "E20.0.17.14", {"start": v(10.38, 1335.09) * mm, "end": v(10.38, 1331.91) * mm});
            skPoint(sketch, "E20.0.18.0", {"position": v(15.14, 1428.75) * mm});
            skArc(sketch, "E20.0.18.1", {"start": v(19.9, 1430.34) * mm, "mid": v(15.14, 1435.1) * mm, "end": v(10.38, 1430.34) * mm});
            skPoint(sketch, "E20.0.18.2", {"position": v(15.14, 1409.7) * mm});
            skPoint(sketch, "E20.0.18.3", {"position": v(15.14, 1390.65) * mm});
            skArc(sketch, "E20.0.18.4", {"start": v(10.38, 1427.16) * mm, "mid": v(15.14, 1422.4) * mm, "end": v(19.9, 1427.16) * mm});
            skCircle(sketch, "E20.0.18.5", {"center": v(15.14, 1390.65) * mm, "radius": 4.76 * mm});
            skCircle(sketch, "E20.0.18.6", {"center": v(15.14, 1371.6) * mm, "radius": 4.76 * mm});
            skArc(sketch, "E20.0.18.7", {"start": v(19.9, 1411.29) * mm, "mid": v(15.14, 1416.05) * mm, "end": v(10.38, 1411.29) * mm});
            skArc(sketch, "E20.0.18.8", {"start": v(10.38, 1408.11) * mm, "mid": v(15.14, 1403.35) * mm, "end": v(19.9, 1408.11) * mm});
            skPoint(sketch, "E20.0.18.9", {"position": v(15.14, 1428.75) * mm});
            skPoint(sketch, "E20.0.18.10", {"position": v(15.14, 1409.7) * mm});
            skLineSegment(sketch, "E20.0.18.11", {"start": v(10.38, 1430.34) * mm, "end": v(10.38, 1427.16) * mm});
            skLineSegment(sketch, "E20.0.18.12", {"start": v(19.9, 1430.34) * mm, "end": v(19.9, 1427.16) * mm});
            skLineSegment(sketch, "E20.0.18.13", {"start": v(19.9, 1411.29) * mm, "end": v(19.9, 1408.11) * mm});
            skLineSegment(sketch, "E20.0.18.14", {"start": v(10.38, 1411.29) * mm, "end": v(10.38, 1408.11) * mm});
            skPoint(sketch, "E20.0.19.0", {"position": v(15.14, 1504.95) * mm});
            skArc(sketch, "E20.0.19.1", {"start": v(19.9, 1506.54) * mm, "mid": v(15.14, 1511.3) * mm, "end": v(10.38, 1506.54) * mm});
            skPoint(sketch, "E20.0.19.2", {"position": v(15.14, 1485.9) * mm});
            skPoint(sketch, "E20.0.19.3", {"position": v(15.14, 1466.85) * mm});
            skArc(sketch, "E20.0.19.4", {"start": v(10.38, 1503.36) * mm, "mid": v(15.14, 1498.6) * mm, "end": v(19.9, 1503.36) * mm});
            skCircle(sketch, "E20.0.19.5", {"center": v(15.14, 1466.85) * mm, "radius": 4.76 * mm});
            skCircle(sketch, "E20.0.19.6", {"center": v(15.14, 1447.8) * mm, "radius": 4.76 * mm});
            skArc(sketch, "E20.0.19.7", {"start": v(19.9, 1487.49) * mm, "mid": v(15.14, 1492.25) * mm, "end": v(10.38, 1487.49) * mm});
            skArc(sketch, "E20.0.19.8", {"start": v(10.38, 1484.31) * mm, "mid": v(15.14, 1479.55) * mm, "end": v(19.9, 1484.31) * mm});
            skPoint(sketch, "E20.0.19.9", {"position": v(15.14, 1504.95) * mm});
            skPoint(sketch, "E20.0.19.10", {"position": v(15.14, 1485.9) * mm});
            skLineSegment(sketch, "E20.0.19.11", {"start": v(10.38, 1506.54) * mm, "end": v(10.38, 1503.36) * mm});
            skLineSegment(sketch, "E20.0.19.12", {"start": v(19.9, 1506.54) * mm, "end": v(19.9, 1503.36) * mm});
            skLineSegment(sketch, "E20.0.19.13", {"start": v(19.9, 1487.49) * mm, "end": v(19.9, 1484.31) * mm});
            skLineSegment(sketch, "E20.0.19.14", {"start": v(10.38, 1487.49) * mm, "end": v(10.38, 1484.31) * mm});
            skPoint(sketch, "E20.0.20.0", {"position": v(15.14, 1581.15) * mm});
            skArc(sketch, "E20.0.20.1", {"start": v(19.9, 1582.74) * mm, "mid": v(15.14, 1587.5) * mm, "end": v(10.38, 1582.74) * mm});
            skPoint(sketch, "E20.0.20.2", {"position": v(15.14, 1562.1) * mm});
            skPoint(sketch, "E20.0.20.3", {"position": v(15.14, 1543.05) * mm});
            skArc(sketch, "E20.0.20.4", {"start": v(10.38, 1579.56) * mm, "mid": v(15.14, 1574.8) * mm, "end": v(19.9, 1579.56) * mm});
            skCircle(sketch, "E20.0.20.5", {"center": v(15.14, 1543.05) * mm, "radius": 4.76 * mm});
            skCircle(sketch, "E20.0.20.6", {"center": v(15.14, 1524) * mm, "radius": 4.76 * mm});
            skArc(sketch, "E20.0.20.7", {"start": v(19.9, 1563.69) * mm, "mid": v(15.14, 1568.45) * mm, "end": v(10.38, 1563.69) * mm});
            skArc(sketch, "E20.0.20.8", {"start": v(10.38, 1560.51) * mm, "mid": v(15.14, 1555.75) * mm, "end": v(19.9, 1560.51) * mm});
            skPoint(sketch, "E20.0.20.9", {"position": v(15.14, 1581.15) * mm});
            skPoint(sketch, "E20.0.20.10", {"position": v(15.14, 1562.1) * mm});
            skLineSegment(sketch, "E20.0.20.11", {"start": v(10.38, 1582.74) * mm, "end": v(10.38, 1579.56) * mm});
            skLineSegment(sketch, "E20.0.20.12", {"start": v(19.9, 1582.74) * mm, "end": v(19.9, 1579.56) * mm});
            skLineSegment(sketch, "E20.0.20.13", {"start": v(19.9, 1563.69) * mm, "end": v(19.9, 1560.51) * mm});
            skLineSegment(sketch, "E20.0.20.14", {"start": v(10.38, 1563.69) * mm, "end": v(10.38, 1560.51) * mm});
            skPoint(sketch, "E20.0.21.0", {"position": v(15.14, 1657.35) * mm});
            skArc(sketch, "E20.0.21.1", {"start": v(19.9, 1658.94) * mm, "mid": v(15.14, 1663.7) * mm, "end": v(10.38, 1658.94) * mm});
            skPoint(sketch, "E20.0.21.2", {"position": v(15.14, 1638.3) * mm});
            skPoint(sketch, "E20.0.21.3", {"position": v(15.14, 1619.25) * mm});
            skArc(sketch, "E20.0.21.4", {"start": v(10.38, 1655.76) * mm, "mid": v(15.14, 1651) * mm, "end": v(19.9, 1655.76) * mm});
            skCircle(sketch, "E20.0.21.5", {"center": v(15.14, 1619.25) * mm, "radius": 4.76 * mm});
            skCircle(sketch, "E20.0.21.6", {"center": v(15.14, 1600.2) * mm, "radius": 4.76 * mm});
            skArc(sketch, "E20.0.21.7", {"start": v(19.9, 1639.89) * mm, "mid": v(15.14, 1644.65) * mm, "end": v(10.38, 1639.89) * mm});
            skArc(sketch, "E20.0.21.8", {"start": v(10.38, 1636.71) * mm, "mid": v(15.14, 1631.95) * mm, "end": v(19.9, 1636.71) * mm});
            skPoint(sketch, "E20.0.21.9", {"position": v(15.14, 1657.35) * mm});
            skPoint(sketch, "E20.0.21.10", {"position": v(15.14, 1638.3) * mm});
            skLineSegment(sketch, "E20.0.21.11", {"start": v(10.38, 1658.94) * mm, "end": v(10.38, 1655.76) * mm});
            skLineSegment(sketch, "E20.0.21.12", {"start": v(19.9, 1658.94) * mm, "end": v(19.9, 1655.76) * mm});
            skLineSegment(sketch, "E20.0.21.13", {"start": v(19.9, 1639.89) * mm, "end": v(19.9, 1636.71) * mm});
            skLineSegment(sketch, "E20.0.21.14", {"start": v(10.38, 1639.89) * mm, "end": v(10.38, 1636.71) * mm});
            skPoint(sketch, "E20.0.22.0", {"position": v(15.14, 1733.55) * mm});
            skArc(sketch, "E20.0.22.1", {"start": v(19.9, 1735.14) * mm, "mid": v(15.14, 1739.9) * mm, "end": v(10.38, 1735.14) * mm});
            skPoint(sketch, "E20.0.22.2", {"position": v(15.14, 1714.5) * mm});
            skPoint(sketch, "E20.0.22.3", {"position": v(15.14, 1695.45) * mm});
            skArc(sketch, "E20.0.22.4", {"start": v(10.38, 1731.96) * mm, "mid": v(15.14, 1727.2) * mm, "end": v(19.9, 1731.96) * mm});
            skCircle(sketch, "E20.0.22.5", {"center": v(15.14, 1695.45) * mm, "radius": 4.76 * mm});
            skCircle(sketch, "E20.0.22.6", {"center": v(15.14, 1676.4) * mm, "radius": 4.76 * mm});
            skArc(sketch, "E20.0.22.7", {"start": v(19.9, 1716.09) * mm, "mid": v(15.14, 1720.85) * mm, "end": v(10.38, 1716.09) * mm});
            skArc(sketch, "E20.0.22.8", {"start": v(10.38, 1712.91) * mm, "mid": v(15.14, 1708.15) * mm, "end": v(19.9, 1712.91) * mm});
            skPoint(sketch, "E20.0.22.9", {"position": v(15.14, 1733.55) * mm});
            skPoint(sketch, "E20.0.22.10", {"position": v(15.14, 1714.5) * mm});
            skLineSegment(sketch, "E20.0.22.11", {"start": v(10.38, 1735.14) * mm, "end": v(10.38, 1731.96) * mm});
            skLineSegment(sketch, "E20.0.22.12", {"start": v(19.9, 1735.14) * mm, "end": v(19.9, 1731.96) * mm});
            skLineSegment(sketch, "E20.0.22.13", {"start": v(19.9, 1716.09) * mm, "end": v(19.9, 1712.91) * mm});
            skLineSegment(sketch, "E20.0.22.14", {"start": v(10.38, 1716.09) * mm, "end": v(10.38, 1712.91) * mm});
            skPoint(sketch, "E20.0.23.0", {"position": v(15.14, 1809.75) * mm});
            skArc(sketch, "E20.0.23.1", {"start": v(19.9, 1811.34) * mm, "mid": v(15.14, 1816.1) * mm, "end": v(10.38, 1811.34) * mm});
            skPoint(sketch, "E20.0.23.2", {"position": v(15.14, 1790.7) * mm});
            skPoint(sketch, "E20.0.23.3", {"position": v(15.14, 1771.65) * mm});
            skArc(sketch, "E20.0.23.4", {"start": v(10.38, 1808.16) * mm, "mid": v(15.14, 1803.4) * mm, "end": v(19.9, 1808.16) * mm});
            skCircle(sketch, "E20.0.23.5", {"center": v(15.14, 1771.65) * mm, "radius": 4.76 * mm});
            skCircle(sketch, "E20.0.23.6", {"center": v(15.14, 1752.6) * mm, "radius": 4.76 * mm});
            skArc(sketch, "E20.0.23.7", {"start": v(19.9, 1792.29) * mm, "mid": v(15.14, 1797.05) * mm, "end": v(10.38, 1792.29) * mm});
            skArc(sketch, "E20.0.23.8", {"start": v(10.38, 1789.11) * mm, "mid": v(15.14, 1784.35) * mm, "end": v(19.9, 1789.11) * mm});
            skPoint(sketch, "E20.0.23.9", {"position": v(15.14, 1809.75) * mm});
            skPoint(sketch, "E20.0.23.10", {"position": v(15.14, 1790.7) * mm});
            skLineSegment(sketch, "E20.0.23.11", {"start": v(10.38, 1811.34) * mm, "end": v(10.38, 1808.16) * mm});
            skLineSegment(sketch, "E20.0.23.12", {"start": v(19.9, 1811.34) * mm, "end": v(19.9, 1808.16) * mm});
            skLineSegment(sketch, "E20.0.23.13", {"start": v(19.9, 1792.29) * mm, "end": v(19.9, 1789.11) * mm});
            skLineSegment(sketch, "E20.0.23.14", {"start": v(10.38, 1792.29) * mm, "end": v(10.38, 1789.11) * mm});
            skLineSegment(sketch, "E20.direction1", {"start": v(15.14, 0) * mm, "end": v(40.54, 0) * mm, "construction": true});
            skLineSegment(sketch, "E20.direction2", {"start": v(15.14, 0) * mm, "end": v(15.14, 76.2) * mm, "construction": true});
            skSolve(sketch);
        }
        {
            var Q0;
            Q0=makeQuery(id+"F2.opExtrude","SWEPT_FACE",FACE,{"disambiguationData":[OSD([sQuery(id+"F1.wireOp",EDGE,"E4")])]});
            var sketch = newSketch(context, id + "F4", { "sketchPlane" : qUnion([Q0])});
            skPoint(sketch, "E21", {"position": v(-15.14, 19.05) * mm});
            skLineSegment(sketch, "E22", {"start": v(-15.14, 0) * mm, "end": v(-15.14, 533.4) * mm, "construction": true});
            skCircle(sketch, "E23", {"center": v(-15.14, 19.05) * mm, "radius": 4.76 * mm});
            skCircle(sketch, "E24", {"center": v(-15.14, 0) * mm, "radius": 4.76 * mm});
            skPoint(sketch, "E25", {"position": v(-15.14, 38.1) * mm});
            skPoint(sketch, "E26", {"position": v(-15.14, 57.15) * mm});
            skArc(sketch, "E27", {"start": v(-10.38, 39.69) * mm, "mid": v(-15.14, 44.45) * mm, "end": v(-19.9, 39.69) * mm});
            skArc(sketch, "E28", {"start": v(-19.9, 36.51) * mm, "mid": v(-15.14, 31.75) * mm, "end": v(-10.38, 36.51) * mm});
            skLineSegment(sketch, "E29", {"start": v(-10.38, 39.69) * mm, "end": v(-10.38, 36.51) * mm});
            skLineSegment(sketch, "E30", {"start": v(-19.9, 39.69) * mm, "end": v(-19.9, 36.51) * mm});
            skArc(sketch, "E31", {"start": v(-10.38, 58.74) * mm, "mid": v(-15.14, 63.5) * mm, "end": v(-19.9, 58.74) * mm});
            skArc(sketch, "E32", {"start": v(-19.9, 55.56) * mm, "mid": v(-15.14, 50.8) * mm, "end": v(-10.38, 55.56) * mm});
            skLineSegment(sketch, "E33", {"start": v(-10.38, 58.74) * mm, "end": v(-10.38, 55.56) * mm});
            skLineSegment(sketch, "E34", {"start": v(-19.9, 58.74) * mm, "end": v(-19.9, 55.56) * mm});
            skPoint(sketch, "E35.0.1.0", {"position": v(-15.14, 133.35) * mm});
            skArc(sketch, "E35.0.1.1", {"start": v(-10.38, 134.94) * mm, "mid": v(-15.14, 139.7) * mm, "end": v(-19.9, 134.94) * mm});
            skPoint(sketch, "E35.0.1.2", {"position": v(-15.14, 114.3) * mm});
            skPoint(sketch, "E35.0.1.3", {"position": v(-15.14, 95.25) * mm});
            skArc(sketch, "E35.0.1.4", {"start": v(-19.9, 131.76) * mm, "mid": v(-15.14, 127) * mm, "end": v(-10.38, 131.76) * mm});
            skCircle(sketch, "E35.0.1.5", {"center": v(-15.14, 95.25) * mm, "radius": 4.76 * mm});
            skCircle(sketch, "E35.0.1.6", {"center": v(-15.14, 76.2) * mm, "radius": 4.76 * mm});
            skArc(sketch, "E35.0.1.7", {"start": v(-10.38, 115.89) * mm, "mid": v(-15.14, 120.65) * mm, "end": v(-19.9, 115.89) * mm});
            skArc(sketch, "E35.0.1.8", {"start": v(-19.9, 112.71) * mm, "mid": v(-15.14, 107.95) * mm, "end": v(-10.38, 112.71) * mm});
            skPoint(sketch, "E35.0.1.9", {"position": v(-15.14, 133.35) * mm});
            skPoint(sketch, "E35.0.1.10", {"position": v(-15.14, 114.3) * mm});
            skLineSegment(sketch, "E35.0.1.11", {"start": v(-19.9, 134.94) * mm, "end": v(-19.9, 131.76) * mm});
            skLineSegment(sketch, "E35.0.1.12", {"start": v(-10.38, 134.94) * mm, "end": v(-10.38, 131.76) * mm});
            skLineSegment(sketch, "E35.0.1.13", {"start": v(-10.38, 115.89) * mm, "end": v(-10.38, 112.71) * mm});
            skLineSegment(sketch, "E35.0.1.14", {"start": v(-19.9, 115.89) * mm, "end": v(-19.9, 112.71) * mm});
            skPoint(sketch, "E35.0.2.0", {"position": v(-15.14, 209.55) * mm});
            skArc(sketch, "E35.0.2.1", {"start": v(-10.38, 211.14) * mm, "mid": v(-15.14, 215.9) * mm, "end": v(-19.9, 211.14) * mm});
            skPoint(sketch, "E35.0.2.2", {"position": v(-15.14, 190.5) * mm});
            skPoint(sketch, "E35.0.2.3", {"position": v(-15.14, 171.45) * mm});
            skArc(sketch, "E35.0.2.4", {"start": v(-19.9, 207.96) * mm, "mid": v(-15.14, 203.2) * mm, "end": v(-10.38, 207.96) * mm});
            skCircle(sketch, "E35.0.2.5", {"center": v(-15.14, 171.45) * mm, "radius": 4.76 * mm});
            skCircle(sketch, "E35.0.2.6", {"center": v(-15.14, 152.4) * mm, "radius": 4.76 * mm});
            skArc(sketch, "E35.0.2.7", {"start": v(-10.38, 192.09) * mm, "mid": v(-15.14, 196.85) * mm, "end": v(-19.9, 192.09) * mm});
            skArc(sketch, "E35.0.2.8", {"start": v(-19.9, 188.91) * mm, "mid": v(-15.14, 184.15) * mm, "end": v(-10.38, 188.91) * mm});
            skPoint(sketch, "E35.0.2.9", {"position": v(-15.14, 209.55) * mm});
            skPoint(sketch, "E35.0.2.10", {"position": v(-15.14, 190.5) * mm});
            skLineSegment(sketch, "E35.0.2.11", {"start": v(-19.9, 211.14) * mm, "end": v(-19.9, 207.96) * mm});
            skLineSegment(sketch, "E35.0.2.12", {"start": v(-10.38, 211.14) * mm, "end": v(-10.38, 207.96) * mm});
            skLineSegment(sketch, "E35.0.2.13", {"start": v(-10.38, 192.09) * mm, "end": v(-10.38, 188.91) * mm});
            skLineSegment(sketch, "E35.0.2.14", {"start": v(-19.9, 192.09) * mm, "end": v(-19.9, 188.91) * mm});
            skPoint(sketch, "E35.0.3.0", {"position": v(-15.14, 285.75) * mm});
            skArc(sketch, "E35.0.3.1", {"start": v(-10.38, 287.34) * mm, "mid": v(-15.14, 292.1) * mm, "end": v(-19.9, 287.34) * mm});
            skPoint(sketch, "E35.0.3.2", {"position": v(-15.14, 266.7) * mm});
            skPoint(sketch, "E35.0.3.3", {"position": v(-15.14, 247.65) * mm});
            skArc(sketch, "E35.0.3.4", {"start": v(-19.9, 284.16) * mm, "mid": v(-15.14, 279.4) * mm, "end": v(-10.38, 284.16) * mm});
            skCircle(sketch, "E35.0.3.5", {"center": v(-15.14, 247.65) * mm, "radius": 4.76 * mm});
            skCircle(sketch, "E35.0.3.6", {"center": v(-15.14, 228.6) * mm, "radius": 4.76 * mm});
            skArc(sketch, "E35.0.3.7", {"start": v(-10.38, 268.29) * mm, "mid": v(-15.14, 273.05) * mm, "end": v(-19.9, 268.29) * mm});
            skArc(sketch, "E35.0.3.8", {"start": v(-19.9, 265.11) * mm, "mid": v(-15.14, 260.35) * mm, "end": v(-10.38, 265.11) * mm});
            skPoint(sketch, "E35.0.3.9", {"position": v(-15.14, 285.75) * mm});
            skPoint(sketch, "E35.0.3.10", {"position": v(-15.14, 266.7) * mm});
            skLineSegment(sketch, "E35.0.3.11", {"start": v(-19.9, 287.34) * mm, "end": v(-19.9, 284.16) * mm});
            skLineSegment(sketch, "E35.0.3.12", {"start": v(-10.38, 287.34) * mm, "end": v(-10.38, 284.16) * mm});
            skLineSegment(sketch, "E35.0.3.13", {"start": v(-10.38, 268.29) * mm, "end": v(-10.38, 265.11) * mm});
            skLineSegment(sketch, "E35.0.3.14", {"start": v(-19.9, 268.29) * mm, "end": v(-19.9, 265.11) * mm});
            skPoint(sketch, "E35.0.4.0", {"position": v(-15.14, 361.95) * mm});
            skArc(sketch, "E35.0.4.1", {"start": v(-10.38, 363.54) * mm, "mid": v(-15.14, 368.3) * mm, "end": v(-19.9, 363.54) * mm});
            skPoint(sketch, "E35.0.4.2", {"position": v(-15.14, 342.9) * mm});
            skPoint(sketch, "E35.0.4.3", {"position": v(-15.14, 323.85) * mm});
            skArc(sketch, "E35.0.4.4", {"start": v(-19.9, 360.36) * mm, "mid": v(-15.14, 355.6) * mm, "end": v(-10.38, 360.36) * mm});
            skCircle(sketch, "E35.0.4.5", {"center": v(-15.14, 323.85) * mm, "radius": 4.76 * mm});
            skCircle(sketch, "E35.0.4.6", {"center": v(-15.14, 304.8) * mm, "radius": 4.76 * mm});
            skArc(sketch, "E35.0.4.7", {"start": v(-10.38, 344.49) * mm, "mid": v(-15.14, 349.25) * mm, "end": v(-19.9, 344.49) * mm});
            skArc(sketch, "E35.0.4.8", {"start": v(-19.9, 341.31) * mm, "mid": v(-15.14, 336.55) * mm, "end": v(-10.38, 341.31) * mm});
            skPoint(sketch, "E35.0.4.9", {"position": v(-15.14, 361.95) * mm});
            skPoint(sketch, "E35.0.4.10", {"position": v(-15.14, 342.9) * mm});
            skLineSegment(sketch, "E35.0.4.11", {"start": v(-19.9, 363.54) * mm, "end": v(-19.9, 360.36) * mm});
            skLineSegment(sketch, "E35.0.4.12", {"start": v(-10.38, 363.54) * mm, "end": v(-10.38, 360.36) * mm});
            skLineSegment(sketch, "E35.0.4.13", {"start": v(-10.38, 344.49) * mm, "end": v(-10.38, 341.31) * mm});
            skLineSegment(sketch, "E35.0.4.14", {"start": v(-19.9, 344.49) * mm, "end": v(-19.9, 341.31) * mm});
            skPoint(sketch, "E35.0.5.0", {"position": v(-15.14, 438.15) * mm});
            skArc(sketch, "E35.0.5.1", {"start": v(-10.38, 439.74) * mm, "mid": v(-15.14, 444.5) * mm, "end": v(-19.9, 439.74) * mm});
            skPoint(sketch, "E35.0.5.2", {"position": v(-15.14, 419.1) * mm});
            skPoint(sketch, "E35.0.5.3", {"position": v(-15.14, 400.05) * mm});
            skArc(sketch, "E35.0.5.4", {"start": v(-19.9, 436.56) * mm, "mid": v(-15.14, 431.8) * mm, "end": v(-10.38, 436.56) * mm});
            skCircle(sketch, "E35.0.5.5", {"center": v(-15.14, 400.05) * mm, "radius": 4.76 * mm});
            skCircle(sketch, "E35.0.5.6", {"center": v(-15.14, 381) * mm, "radius": 4.76 * mm});
            skArc(sketch, "E35.0.5.7", {"start": v(-10.38, 420.69) * mm, "mid": v(-15.14, 425.45) * mm, "end": v(-19.9, 420.69) * mm});
            skArc(sketch, "E35.0.5.8", {"start": v(-19.9, 417.51) * mm, "mid": v(-15.14, 412.75) * mm, "end": v(-10.38, 417.51) * mm});
            skPoint(sketch, "E35.0.5.9", {"position": v(-15.14, 438.15) * mm});
            skPoint(sketch, "E35.0.5.10", {"position": v(-15.14, 419.1) * mm});
            skLineSegment(sketch, "E35.0.5.11", {"start": v(-19.9, 439.74) * mm, "end": v(-19.9, 436.56) * mm});
            skLineSegment(sketch, "E35.0.5.12", {"start": v(-10.38, 439.74) * mm, "end": v(-10.38, 436.56) * mm});
            skLineSegment(sketch, "E35.0.5.13", {"start": v(-10.38, 420.69) * mm, "end": v(-10.38, 417.51) * mm});
            skLineSegment(sketch, "E35.0.5.14", {"start": v(-19.9, 420.69) * mm, "end": v(-19.9, 417.51) * mm});
            skPoint(sketch, "E35.0.6.0", {"position": v(-15.14, 514.35) * mm});
            skArc(sketch, "E35.0.6.1", {"start": v(-10.38, 515.94) * mm, "mid": v(-15.14, 520.7) * mm, "end": v(-19.9, 515.94) * mm});
            skPoint(sketch, "E35.0.6.2", {"position": v(-15.14, 495.3) * mm});
            skPoint(sketch, "E35.0.6.3", {"position": v(-15.14, 476.25) * mm});
            skArc(sketch, "E35.0.6.4", {"start": v(-19.9, 512.76) * mm, "mid": v(-15.14, 508) * mm, "end": v(-10.38, 512.76) * mm});
            skCircle(sketch, "E35.0.6.5", {"center": v(-15.14, 476.25) * mm, "radius": 4.76 * mm});
            skCircle(sketch, "E35.0.6.6", {"center": v(-15.14, 457.2) * mm, "radius": 4.76 * mm});
            skArc(sketch, "E35.0.6.7", {"start": v(-10.38, 496.89) * mm, "mid": v(-15.14, 501.65) * mm, "end": v(-19.9, 496.89) * mm});
            skArc(sketch, "E35.0.6.8", {"start": v(-19.9, 493.71) * mm, "mid": v(-15.14, 488.95) * mm, "end": v(-10.38, 493.71) * mm});
            skPoint(sketch, "E35.0.6.9", {"position": v(-15.14, 514.35) * mm});
            skPoint(sketch, "E35.0.6.10", {"position": v(-15.14, 495.3) * mm});
            skLineSegment(sketch, "E35.0.6.11", {"start": v(-19.9, 515.94) * mm, "end": v(-19.9, 512.76) * mm});
            skLineSegment(sketch, "E35.0.6.12", {"start": v(-10.38, 515.94) * mm, "end": v(-10.38, 512.76) * mm});
            skLineSegment(sketch, "E35.0.6.13", {"start": v(-10.38, 496.89) * mm, "end": v(-10.38, 493.71) * mm});
            skLineSegment(sketch, "E35.0.6.14", {"start": v(-19.9, 496.89) * mm, "end": v(-19.9, 493.71) * mm});
            skPoint(sketch, "E35.0.7.0", {"position": v(-15.14, 590.55) * mm});
            skArc(sketch, "E35.0.7.1", {"start": v(-10.38, 592.14) * mm, "mid": v(-15.14, 596.9) * mm, "end": v(-19.9, 592.14) * mm});
            skPoint(sketch, "E35.0.7.2", {"position": v(-15.14, 571.5) * mm});
            skPoint(sketch, "E35.0.7.3", {"position": v(-15.14, 552.45) * mm});
            skArc(sketch, "E35.0.7.4", {"start": v(-19.9, 588.96) * mm, "mid": v(-15.14, 584.2) * mm, "end": v(-10.38, 588.96) * mm});
            skCircle(sketch, "E35.0.7.5", {"center": v(-15.14, 552.45) * mm, "radius": 4.76 * mm});
            skCircle(sketch, "E35.0.7.6", {"center": v(-15.14, 533.4) * mm, "radius": 4.76 * mm});
            skArc(sketch, "E35.0.7.7", {"start": v(-10.38, 573.09) * mm, "mid": v(-15.14, 577.85) * mm, "end": v(-19.9, 573.09) * mm});
            skArc(sketch, "E35.0.7.8", {"start": v(-19.9, 569.91) * mm, "mid": v(-15.14, 565.15) * mm, "end": v(-10.38, 569.91) * mm});
            skPoint(sketch, "E35.0.7.9", {"position": v(-15.14, 590.55) * mm});
            skPoint(sketch, "E35.0.7.10", {"position": v(-15.14, 571.5) * mm});
            skLineSegment(sketch, "E35.0.7.11", {"start": v(-19.9, 592.14) * mm, "end": v(-19.9, 588.96) * mm});
            skLineSegment(sketch, "E35.0.7.12", {"start": v(-10.38, 592.14) * mm, "end": v(-10.38, 588.96) * mm});
            skLineSegment(sketch, "E35.0.7.13", {"start": v(-10.38, 573.09) * mm, "end": v(-10.38, 569.91) * mm});
            skLineSegment(sketch, "E35.0.7.14", {"start": v(-19.9, 573.09) * mm, "end": v(-19.9, 569.91) * mm});
            skPoint(sketch, "E35.0.8.0", {"position": v(-15.14, 666.75) * mm});
            skArc(sketch, "E35.0.8.1", {"start": v(-10.38, 668.34) * mm, "mid": v(-15.14, 673.1) * mm, "end": v(-19.9, 668.34) * mm});
            skPoint(sketch, "E35.0.8.2", {"position": v(-15.14, 647.7) * mm});
            skPoint(sketch, "E35.0.8.3", {"position": v(-15.14, 628.65) * mm});
            skArc(sketch, "E35.0.8.4", {"start": v(-19.9, 665.16) * mm, "mid": v(-15.14, 660.4) * mm, "end": v(-10.38, 665.16) * mm});
            skCircle(sketch, "E35.0.8.5", {"center": v(-15.14, 628.65) * mm, "radius": 4.76 * mm});
            skCircle(sketch, "E35.0.8.6", {"center": v(-15.14, 609.6) * mm, "radius": 4.76 * mm});
            skArc(sketch, "E35.0.8.7", {"start": v(-10.38, 649.29) * mm, "mid": v(-15.14, 654.05) * mm, "end": v(-19.9, 649.29) * mm});
            skArc(sketch, "E35.0.8.8", {"start": v(-19.9, 646.11) * mm, "mid": v(-15.14, 641.35) * mm, "end": v(-10.38, 646.11) * mm});
            skPoint(sketch, "E35.0.8.9", {"position": v(-15.14, 666.75) * mm});
            skPoint(sketch, "E35.0.8.10", {"position": v(-15.14, 647.7) * mm});
            skLineSegment(sketch, "E35.0.8.11", {"start": v(-19.9, 668.34) * mm, "end": v(-19.9, 665.16) * mm});
            skLineSegment(sketch, "E35.0.8.12", {"start": v(-10.38, 668.34) * mm, "end": v(-10.38, 665.16) * mm});
            skLineSegment(sketch, "E35.0.8.13", {"start": v(-10.38, 649.29) * mm, "end": v(-10.38, 646.11) * mm});
            skLineSegment(sketch, "E35.0.8.14", {"start": v(-19.9, 649.29) * mm, "end": v(-19.9, 646.11) * mm});
            skPoint(sketch, "E35.0.9.0", {"position": v(-15.14, 742.95) * mm});
            skArc(sketch, "E35.0.9.1", {"start": v(-10.38, 744.54) * mm, "mid": v(-15.14, 749.3) * mm, "end": v(-19.9, 744.54) * mm});
            skPoint(sketch, "E35.0.9.2", {"position": v(-15.14, 723.9) * mm});
            skPoint(sketch, "E35.0.9.3", {"position": v(-15.14, 704.85) * mm});
            skArc(sketch, "E35.0.9.4", {"start": v(-19.9, 741.36) * mm, "mid": v(-15.14, 736.6) * mm, "end": v(-10.38, 741.36) * mm});
            skCircle(sketch, "E35.0.9.5", {"center": v(-15.14, 704.85) * mm, "radius": 4.76 * mm});
            skCircle(sketch, "E35.0.9.6", {"center": v(-15.14, 685.8) * mm, "radius": 4.76 * mm});
            skArc(sketch, "E35.0.9.7", {"start": v(-10.38, 725.49) * mm, "mid": v(-15.14, 730.25) * mm, "end": v(-19.9, 725.49) * mm});
            skArc(sketch, "E35.0.9.8", {"start": v(-19.9, 722.31) * mm, "mid": v(-15.14, 717.55) * mm, "end": v(-10.38, 722.31) * mm});
            skPoint(sketch, "E35.0.9.9", {"position": v(-15.14, 742.95) * mm});
            skPoint(sketch, "E35.0.9.10", {"position": v(-15.14, 723.9) * mm});
            skLineSegment(sketch, "E35.0.9.11", {"start": v(-19.9, 744.54) * mm, "end": v(-19.9, 741.36) * mm});
            skLineSegment(sketch, "E35.0.9.12", {"start": v(-10.38, 744.54) * mm, "end": v(-10.38, 741.36) * mm});
            skLineSegment(sketch, "E35.0.9.13", {"start": v(-10.38, 725.49) * mm, "end": v(-10.38, 722.31) * mm});
            skLineSegment(sketch, "E35.0.9.14", {"start": v(-19.9, 725.49) * mm, "end": v(-19.9, 722.31) * mm});
            skPoint(sketch, "E35.0.10.0", {"position": v(-15.14, 819.15) * mm});
            skArc(sketch, "E35.0.10.1", {"start": v(-10.38, 820.74) * mm, "mid": v(-15.14, 825.5) * mm, "end": v(-19.9, 820.74) * mm});
            skPoint(sketch, "E35.0.10.2", {"position": v(-15.14, 800.1) * mm});
            skPoint(sketch, "E35.0.10.3", {"position": v(-15.14, 781.05) * mm});
            skArc(sketch, "E35.0.10.4", {"start": v(-19.9, 817.56) * mm, "mid": v(-15.14, 812.8) * mm, "end": v(-10.38, 817.56) * mm});
            skCircle(sketch, "E35.0.10.5", {"center": v(-15.14, 781.05) * mm, "radius": 4.76 * mm});
            skCircle(sketch, "E35.0.10.6", {"center": v(-15.14, 762) * mm, "radius": 4.76 * mm});
            skArc(sketch, "E35.0.10.7", {"start": v(-10.38, 801.69) * mm, "mid": v(-15.14, 806.45) * mm, "end": v(-19.9, 801.69) * mm});
            skArc(sketch, "E35.0.10.8", {"start": v(-19.9, 798.51) * mm, "mid": v(-15.14, 793.75) * mm, "end": v(-10.38, 798.51) * mm});
            skPoint(sketch, "E35.0.10.9", {"position": v(-15.14, 819.15) * mm});
            skPoint(sketch, "E35.0.10.10", {"position": v(-15.14, 800.1) * mm});
            skLineSegment(sketch, "E35.0.10.11", {"start": v(-19.9, 820.74) * mm, "end": v(-19.9, 817.56) * mm});
            skLineSegment(sketch, "E35.0.10.12", {"start": v(-10.38, 820.74) * mm, "end": v(-10.38, 817.56) * mm});
            skLineSegment(sketch, "E35.0.10.13", {"start": v(-10.38, 801.69) * mm, "end": v(-10.38, 798.51) * mm});
            skLineSegment(sketch, "E35.0.10.14", {"start": v(-19.9, 801.69) * mm, "end": v(-19.9, 798.51) * mm});
            skPoint(sketch, "E35.0.11.0", {"position": v(-15.14, 895.35) * mm});
            skArc(sketch, "E35.0.11.1", {"start": v(-10.38, 896.94) * mm, "mid": v(-15.14, 901.7) * mm, "end": v(-19.9, 896.94) * mm});
            skPoint(sketch, "E35.0.11.2", {"position": v(-15.14, 876.3) * mm});
            skPoint(sketch, "E35.0.11.3", {"position": v(-15.14, 857.25) * mm});
            skArc(sketch, "E35.0.11.4", {"start": v(-19.9, 893.76) * mm, "mid": v(-15.14, 889) * mm, "end": v(-10.38, 893.76) * mm});
            skCircle(sketch, "E35.0.11.5", {"center": v(-15.14, 857.25) * mm, "radius": 4.76 * mm});
            skCircle(sketch, "E35.0.11.6", {"center": v(-15.14, 838.2) * mm, "radius": 4.76 * mm});
            skArc(sketch, "E35.0.11.7", {"start": v(-10.38, 877.89) * mm, "mid": v(-15.14, 882.65) * mm, "end": v(-19.9, 877.89) * mm});
            skArc(sketch, "E35.0.11.8", {"start": v(-19.9, 874.71) * mm, "mid": v(-15.14, 869.95) * mm, "end": v(-10.38, 874.71) * mm});
            skPoint(sketch, "E35.0.11.9", {"position": v(-15.14, 895.35) * mm});
            skPoint(sketch, "E35.0.11.10", {"position": v(-15.14, 876.3) * mm});
            skLineSegment(sketch, "E35.0.11.11", {"start": v(-19.9, 896.94) * mm, "end": v(-19.9, 893.76) * mm});
            skLineSegment(sketch, "E35.0.11.12", {"start": v(-10.38, 896.94) * mm, "end": v(-10.38, 893.76) * mm});
            skLineSegment(sketch, "E35.0.11.13", {"start": v(-10.38, 877.89) * mm, "end": v(-10.38, 874.71) * mm});
            skLineSegment(sketch, "E35.0.11.14", {"start": v(-19.9, 877.89) * mm, "end": v(-19.9, 874.71) * mm});
            skPoint(sketch, "E35.0.12.0", {"position": v(-15.14, 971.55) * mm});
            skArc(sketch, "E35.0.12.1", {"start": v(-10.38, 973.14) * mm, "mid": v(-15.14, 977.9) * mm, "end": v(-19.9, 973.14) * mm});
            skPoint(sketch, "E35.0.12.2", {"position": v(-15.14, 952.5) * mm});
            skPoint(sketch, "E35.0.12.3", {"position": v(-15.14, 933.45) * mm});
            skArc(sketch, "E35.0.12.4", {"start": v(-19.9, 969.96) * mm, "mid": v(-15.14, 965.2) * mm, "end": v(-10.38, 969.96) * mm});
            skCircle(sketch, "E35.0.12.5", {"center": v(-15.14, 933.45) * mm, "radius": 4.76 * mm});
            skCircle(sketch, "E35.0.12.6", {"center": v(-15.14, 914.4) * mm, "radius": 4.76 * mm});
            skArc(sketch, "E35.0.12.7", {"start": v(-10.38, 954.09) * mm, "mid": v(-15.14, 958.85) * mm, "end": v(-19.9, 954.09) * mm});
            skArc(sketch, "E35.0.12.8", {"start": v(-19.9, 950.91) * mm, "mid": v(-15.14, 946.15) * mm, "end": v(-10.38, 950.91) * mm});
            skPoint(sketch, "E35.0.12.9", {"position": v(-15.14, 971.55) * mm});
            skPoint(sketch, "E35.0.12.10", {"position": v(-15.14, 952.5) * mm});
            skLineSegment(sketch, "E35.0.12.11", {"start": v(-19.9, 973.14) * mm, "end": v(-19.9, 969.96) * mm});
            skLineSegment(sketch, "E35.0.12.12", {"start": v(-10.38, 973.14) * mm, "end": v(-10.38, 969.96) * mm});
            skLineSegment(sketch, "E35.0.12.13", {"start": v(-10.38, 954.09) * mm, "end": v(-10.38, 950.91) * mm});
            skLineSegment(sketch, "E35.0.12.14", {"start": v(-19.9, 954.09) * mm, "end": v(-19.9, 950.91) * mm});
            skPoint(sketch, "E35.0.13.0", {"position": v(-15.14, 1047.75) * mm});
            skArc(sketch, "E35.0.13.1", {"start": v(-10.38, 1049.34) * mm, "mid": v(-15.14, 1054.1) * mm, "end": v(-19.9, 1049.34) * mm});
            skPoint(sketch, "E35.0.13.2", {"position": v(-15.14, 1028.7) * mm});
            skPoint(sketch, "E35.0.13.3", {"position": v(-15.14, 1009.65) * mm});
            skArc(sketch, "E35.0.13.4", {"start": v(-19.9, 1046.16) * mm, "mid": v(-15.14, 1041.4) * mm, "end": v(-10.38, 1046.16) * mm});
            skCircle(sketch, "E35.0.13.5", {"center": v(-15.14, 1009.65) * mm, "radius": 4.76 * mm});
            skCircle(sketch, "E35.0.13.6", {"center": v(-15.14, 990.6) * mm, "radius": 4.76 * mm});
            skArc(sketch, "E35.0.13.7", {"start": v(-10.38, 1030.29) * mm, "mid": v(-15.14, 1035.05) * mm, "end": v(-19.9, 1030.29) * mm});
            skArc(sketch, "E35.0.13.8", {"start": v(-19.9, 1027.11) * mm, "mid": v(-15.14, 1022.35) * mm, "end": v(-10.38, 1027.11) * mm});
            skPoint(sketch, "E35.0.13.9", {"position": v(-15.14, 1047.75) * mm});
            skPoint(sketch, "E35.0.13.10", {"position": v(-15.14, 1028.7) * mm});
            skLineSegment(sketch, "E35.0.13.11", {"start": v(-19.9, 1049.34) * mm, "end": v(-19.9, 1046.16) * mm});
            skLineSegment(sketch, "E35.0.13.12", {"start": v(-10.38, 1049.34) * mm, "end": v(-10.38, 1046.16) * mm});
            skLineSegment(sketch, "E35.0.13.13", {"start": v(-10.38, 1030.29) * mm, "end": v(-10.38, 1027.11) * mm});
            skLineSegment(sketch, "E35.0.13.14", {"start": v(-19.9, 1030.29) * mm, "end": v(-19.9, 1027.11) * mm});
            skPoint(sketch, "E35.0.14.0", {"position": v(-15.14, 1123.95) * mm});
            skArc(sketch, "E35.0.14.1", {"start": v(-10.38, 1125.54) * mm, "mid": v(-15.14, 1130.3) * mm, "end": v(-19.9, 1125.54) * mm});
            skPoint(sketch, "E35.0.14.2", {"position": v(-15.14, 1104.9) * mm});
            skPoint(sketch, "E35.0.14.3", {"position": v(-15.14, 1085.85) * mm});
            skArc(sketch, "E35.0.14.4", {"start": v(-19.9, 1122.36) * mm, "mid": v(-15.14, 1117.6) * mm, "end": v(-10.38, 1122.36) * mm});
            skCircle(sketch, "E35.0.14.5", {"center": v(-15.14, 1085.85) * mm, "radius": 4.76 * mm});
            skCircle(sketch, "E35.0.14.6", {"center": v(-15.14, 1066.8) * mm, "radius": 4.76 * mm});
            skArc(sketch, "E35.0.14.7", {"start": v(-10.38, 1106.49) * mm, "mid": v(-15.14, 1111.25) * mm, "end": v(-19.9, 1106.49) * mm});
            skArc(sketch, "E35.0.14.8", {"start": v(-19.9, 1103.31) * mm, "mid": v(-15.14, 1098.55) * mm, "end": v(-10.38, 1103.31) * mm});
            skPoint(sketch, "E35.0.14.9", {"position": v(-15.14, 1123.95) * mm});
            skPoint(sketch, "E35.0.14.10", {"position": v(-15.14, 1104.9) * mm});
            skLineSegment(sketch, "E35.0.14.11", {"start": v(-19.9, 1125.54) * mm, "end": v(-19.9, 1122.36) * mm});
            skLineSegment(sketch, "E35.0.14.12", {"start": v(-10.38, 1125.54) * mm, "end": v(-10.38, 1122.36) * mm});
            skLineSegment(sketch, "E35.0.14.13", {"start": v(-10.38, 1106.49) * mm, "end": v(-10.38, 1103.31) * mm});
            skLineSegment(sketch, "E35.0.14.14", {"start": v(-19.9, 1106.49) * mm, "end": v(-19.9, 1103.31) * mm});
            skPoint(sketch, "E35.0.15.0", {"position": v(-15.14, 1200.15) * mm});
            skArc(sketch, "E35.0.15.1", {"start": v(-10.38, 1201.74) * mm, "mid": v(-15.14, 1206.5) * mm, "end": v(-19.9, 1201.74) * mm});
            skPoint(sketch, "E35.0.15.2", {"position": v(-15.14, 1181.1) * mm});
            skPoint(sketch, "E35.0.15.3", {"position": v(-15.14, 1162.05) * mm});
            skArc(sketch, "E35.0.15.4", {"start": v(-19.9, 1198.56) * mm, "mid": v(-15.14, 1193.8) * mm, "end": v(-10.38, 1198.56) * mm});
            skCircle(sketch, "E35.0.15.5", {"center": v(-15.14, 1162.05) * mm, "radius": 4.76 * mm});
            skCircle(sketch, "E35.0.15.6", {"center": v(-15.14, 1143) * mm, "radius": 4.76 * mm});
            skArc(sketch, "E35.0.15.7", {"start": v(-10.38, 1182.69) * mm, "mid": v(-15.14, 1187.45) * mm, "end": v(-19.9, 1182.69) * mm});
            skArc(sketch, "E35.0.15.8", {"start": v(-19.9, 1179.51) * mm, "mid": v(-15.14, 1174.75) * mm, "end": v(-10.38, 1179.51) * mm});
            skPoint(sketch, "E35.0.15.9", {"position": v(-15.14, 1200.15) * mm});
            skPoint(sketch, "E35.0.15.10", {"position": v(-15.14, 1181.1) * mm});
            skLineSegment(sketch, "E35.0.15.11", {"start": v(-19.9, 1201.74) * mm, "end": v(-19.9, 1198.56) * mm});
            skLineSegment(sketch, "E35.0.15.12", {"start": v(-10.38, 1201.74) * mm, "end": v(-10.38, 1198.56) * mm});
            skLineSegment(sketch, "E35.0.15.13", {"start": v(-10.38, 1182.69) * mm, "end": v(-10.38, 1179.51) * mm});
            skLineSegment(sketch, "E35.0.15.14", {"start": v(-19.9, 1182.69) * mm, "end": v(-19.9, 1179.51) * mm});
            skPoint(sketch, "E35.0.16.0", {"position": v(-15.14, 1276.35) * mm});
            skArc(sketch, "E35.0.16.1", {"start": v(-10.38, 1277.94) * mm, "mid": v(-15.14, 1282.7) * mm, "end": v(-19.9, 1277.94) * mm});
            skPoint(sketch, "E35.0.16.2", {"position": v(-15.14, 1257.3) * mm});
            skPoint(sketch, "E35.0.16.3", {"position": v(-15.14, 1238.25) * mm});
            skArc(sketch, "E35.0.16.4", {"start": v(-19.9, 1274.76) * mm, "mid": v(-15.14, 1270) * mm, "end": v(-10.38, 1274.76) * mm});
            skCircle(sketch, "E35.0.16.5", {"center": v(-15.14, 1238.25) * mm, "radius": 4.76 * mm});
            skCircle(sketch, "E35.0.16.6", {"center": v(-15.14, 1219.2) * mm, "radius": 4.76 * mm});
            skArc(sketch, "E35.0.16.7", {"start": v(-10.38, 1258.89) * mm, "mid": v(-15.14, 1263.65) * mm, "end": v(-19.9, 1258.89) * mm});
            skArc(sketch, "E35.0.16.8", {"start": v(-19.9, 1255.71) * mm, "mid": v(-15.14, 1250.95) * mm, "end": v(-10.38, 1255.71) * mm});
            skPoint(sketch, "E35.0.16.9", {"position": v(-15.14, 1276.35) * mm});
            skPoint(sketch, "E35.0.16.10", {"position": v(-15.14, 1257.3) * mm});
            skLineSegment(sketch, "E35.0.16.11", {"start": v(-19.9, 1277.94) * mm, "end": v(-19.9, 1274.76) * mm});
            skLineSegment(sketch, "E35.0.16.12", {"start": v(-10.38, 1277.94) * mm, "end": v(-10.38, 1274.76) * mm});
            skLineSegment(sketch, "E35.0.16.13", {"start": v(-10.38, 1258.89) * mm, "end": v(-10.38, 1255.71) * mm});
            skLineSegment(sketch, "E35.0.16.14", {"start": v(-19.9, 1258.89) * mm, "end": v(-19.9, 1255.71) * mm});
            skPoint(sketch, "E35.0.17.0", {"position": v(-15.14, 1352.55) * mm});
            skArc(sketch, "E35.0.17.1", {"start": v(-10.38, 1354.14) * mm, "mid": v(-15.14, 1358.9) * mm, "end": v(-19.9, 1354.14) * mm});
            skPoint(sketch, "E35.0.17.2", {"position": v(-15.14, 1333.5) * mm});
            skPoint(sketch, "E35.0.17.3", {"position": v(-15.14, 1314.45) * mm});
            skArc(sketch, "E35.0.17.4", {"start": v(-19.9, 1350.96) * mm, "mid": v(-15.14, 1346.2) * mm, "end": v(-10.38, 1350.96) * mm});
            skCircle(sketch, "E35.0.17.5", {"center": v(-15.14, 1314.45) * mm, "radius": 4.76 * mm});
            skCircle(sketch, "E35.0.17.6", {"center": v(-15.14, 1295.4) * mm, "radius": 4.76 * mm});
            skArc(sketch, "E35.0.17.7", {"start": v(-10.38, 1335.09) * mm, "mid": v(-15.14, 1339.85) * mm, "end": v(-19.9, 1335.09) * mm});
            skArc(sketch, "E35.0.17.8", {"start": v(-19.9, 1331.91) * mm, "mid": v(-15.14, 1327.15) * mm, "end": v(-10.38, 1331.91) * mm});
            skPoint(sketch, "E35.0.17.9", {"position": v(-15.14, 1352.55) * mm});
            skPoint(sketch, "E35.0.17.10", {"position": v(-15.14, 1333.5) * mm});
            skLineSegment(sketch, "E35.0.17.11", {"start": v(-19.9, 1354.14) * mm, "end": v(-19.9, 1350.96) * mm});
            skLineSegment(sketch, "E35.0.17.12", {"start": v(-10.38, 1354.14) * mm, "end": v(-10.38, 1350.96) * mm});
            skLineSegment(sketch, "E35.0.17.13", {"start": v(-10.38, 1335.09) * mm, "end": v(-10.38, 1331.91) * mm});
            skLineSegment(sketch, "E35.0.17.14", {"start": v(-19.9, 1335.09) * mm, "end": v(-19.9, 1331.91) * mm});
            skPoint(sketch, "E35.0.18.0", {"position": v(-15.14, 1428.75) * mm});
            skArc(sketch, "E35.0.18.1", {"start": v(-10.38, 1430.34) * mm, "mid": v(-15.14, 1435.1) * mm, "end": v(-19.9, 1430.34) * mm});
            skPoint(sketch, "E35.0.18.2", {"position": v(-15.14, 1409.7) * mm});
            skPoint(sketch, "E35.0.18.3", {"position": v(-15.14, 1390.65) * mm});
            skArc(sketch, "E35.0.18.4", {"start": v(-19.9, 1427.16) * mm, "mid": v(-15.14, 1422.4) * mm, "end": v(-10.38, 1427.16) * mm});
            skCircle(sketch, "E35.0.18.5", {"center": v(-15.14, 1390.65) * mm, "radius": 4.76 * mm});
            skCircle(sketch, "E35.0.18.6", {"center": v(-15.14, 1371.6) * mm, "radius": 4.76 * mm});
            skArc(sketch, "E35.0.18.7", {"start": v(-10.38, 1411.29) * mm, "mid": v(-15.14, 1416.05) * mm, "end": v(-19.9, 1411.29) * mm});
            skArc(sketch, "E35.0.18.8", {"start": v(-19.9, 1408.11) * mm, "mid": v(-15.14, 1403.35) * mm, "end": v(-10.38, 1408.11) * mm});
            skPoint(sketch, "E35.0.18.9", {"position": v(-15.14, 1428.75) * mm});
            skPoint(sketch, "E35.0.18.10", {"position": v(-15.14, 1409.7) * mm});
            skLineSegment(sketch, "E35.0.18.11", {"start": v(-19.9, 1430.34) * mm, "end": v(-19.9, 1427.16) * mm});
            skLineSegment(sketch, "E35.0.18.12", {"start": v(-10.38, 1430.34) * mm, "end": v(-10.38, 1427.16) * mm});
            skLineSegment(sketch, "E35.0.18.13", {"start": v(-10.38, 1411.29) * mm, "end": v(-10.38, 1408.11) * mm});
            skLineSegment(sketch, "E35.0.18.14", {"start": v(-19.9, 1411.29) * mm, "end": v(-19.9, 1408.11) * mm});
            skPoint(sketch, "E35.0.19.0", {"position": v(-15.14, 1504.95) * mm});
            skArc(sketch, "E35.0.19.1", {"start": v(-10.38, 1506.54) * mm, "mid": v(-15.14, 1511.3) * mm, "end": v(-19.9, 1506.54) * mm});
            skPoint(sketch, "E35.0.19.2", {"position": v(-15.14, 1485.9) * mm});
            skPoint(sketch, "E35.0.19.3", {"position": v(-15.14, 1466.85) * mm});
            skArc(sketch, "E35.0.19.4", {"start": v(-19.9, 1503.36) * mm, "mid": v(-15.14, 1498.6) * mm, "end": v(-10.38, 1503.36) * mm});
            skCircle(sketch, "E35.0.19.5", {"center": v(-15.14, 1466.85) * mm, "radius": 4.76 * mm});
            skCircle(sketch, "E35.0.19.6", {"center": v(-15.14, 1447.8) * mm, "radius": 4.76 * mm});
            skArc(sketch, "E35.0.19.7", {"start": v(-10.38, 1487.49) * mm, "mid": v(-15.14, 1492.25) * mm, "end": v(-19.9, 1487.49) * mm});
            skArc(sketch, "E35.0.19.8", {"start": v(-19.9, 1484.31) * mm, "mid": v(-15.14, 1479.55) * mm, "end": v(-10.38, 1484.31) * mm});
            skPoint(sketch, "E35.0.19.9", {"position": v(-15.14, 1504.95) * mm});
            skPoint(sketch, "E35.0.19.10", {"position": v(-15.14, 1485.9) * mm});
            skLineSegment(sketch, "E35.0.19.11", {"start": v(-19.9, 1506.54) * mm, "end": v(-19.9, 1503.36) * mm});
            skLineSegment(sketch, "E35.0.19.12", {"start": v(-10.38, 1506.54) * mm, "end": v(-10.38, 1503.36) * mm});
            skLineSegment(sketch, "E35.0.19.13", {"start": v(-10.38, 1487.49) * mm, "end": v(-10.38, 1484.31) * mm});
            skLineSegment(sketch, "E35.0.19.14", {"start": v(-19.9, 1487.49) * mm, "end": v(-19.9, 1484.31) * mm});
            skPoint(sketch, "E35.0.20.0", {"position": v(-15.14, 1581.15) * mm});
            skArc(sketch, "E35.0.20.1", {"start": v(-10.38, 1582.74) * mm, "mid": v(-15.14, 1587.5) * mm, "end": v(-19.9, 1582.74) * mm});
            skPoint(sketch, "E35.0.20.2", {"position": v(-15.14, 1562.1) * mm});
            skPoint(sketch, "E35.0.20.3", {"position": v(-15.14, 1543.05) * mm});
            skArc(sketch, "E35.0.20.4", {"start": v(-19.9, 1579.56) * mm, "mid": v(-15.14, 1574.8) * mm, "end": v(-10.38, 1579.56) * mm});
            skCircle(sketch, "E35.0.20.5", {"center": v(-15.14, 1543.05) * mm, "radius": 4.76 * mm});
            skCircle(sketch, "E35.0.20.6", {"center": v(-15.14, 1524) * mm, "radius": 4.76 * mm});
            skArc(sketch, "E35.0.20.7", {"start": v(-10.38, 1563.69) * mm, "mid": v(-15.14, 1568.45) * mm, "end": v(-19.9, 1563.69) * mm});
            skArc(sketch, "E35.0.20.8", {"start": v(-19.9, 1560.51) * mm, "mid": v(-15.14, 1555.75) * mm, "end": v(-10.38, 1560.51) * mm});
            skPoint(sketch, "E35.0.20.9", {"position": v(-15.14, 1581.15) * mm});
            skPoint(sketch, "E35.0.20.10", {"position": v(-15.14, 1562.1) * mm});
            skLineSegment(sketch, "E35.0.20.11", {"start": v(-19.9, 1582.74) * mm, "end": v(-19.9, 1579.56) * mm});
            skLineSegment(sketch, "E35.0.20.12", {"start": v(-10.38, 1582.74) * mm, "end": v(-10.38, 1579.56) * mm});
            skLineSegment(sketch, "E35.0.20.13", {"start": v(-10.38, 1563.69) * mm, "end": v(-10.38, 1560.51) * mm});
            skLineSegment(sketch, "E35.0.20.14", {"start": v(-19.9, 1563.69) * mm, "end": v(-19.9, 1560.51) * mm});
            skPoint(sketch, "E35.0.21.0", {"position": v(-15.14, 1657.35) * mm});
            skArc(sketch, "E35.0.21.1", {"start": v(-10.38, 1658.94) * mm, "mid": v(-15.14, 1663.7) * mm, "end": v(-19.9, 1658.94) * mm});
            skPoint(sketch, "E35.0.21.2", {"position": v(-15.14, 1638.3) * mm});
            skPoint(sketch, "E35.0.21.3", {"position": v(-15.14, 1619.25) * mm});
            skArc(sketch, "E35.0.21.4", {"start": v(-19.9, 1655.76) * mm, "mid": v(-15.14, 1651) * mm, "end": v(-10.38, 1655.76) * mm});
            skCircle(sketch, "E35.0.21.5", {"center": v(-15.14, 1619.25) * mm, "radius": 4.76 * mm});
            skCircle(sketch, "E35.0.21.6", {"center": v(-15.14, 1600.2) * mm, "radius": 4.76 * mm});
            skArc(sketch, "E35.0.21.7", {"start": v(-10.38, 1639.89) * mm, "mid": v(-15.14, 1644.65) * mm, "end": v(-19.9, 1639.89) * mm});
            skArc(sketch, "E35.0.21.8", {"start": v(-19.9, 1636.71) * mm, "mid": v(-15.14, 1631.95) * mm, "end": v(-10.38, 1636.71) * mm});
            skPoint(sketch, "E35.0.21.9", {"position": v(-15.14, 1657.35) * mm});
            skPoint(sketch, "E35.0.21.10", {"position": v(-15.14, 1638.3) * mm});
            skLineSegment(sketch, "E35.0.21.11", {"start": v(-19.9, 1658.94) * mm, "end": v(-19.9, 1655.76) * mm});
            skLineSegment(sketch, "E35.0.21.12", {"start": v(-10.38, 1658.94) * mm, "end": v(-10.38, 1655.76) * mm});
            skLineSegment(sketch, "E35.0.21.13", {"start": v(-10.38, 1639.89) * mm, "end": v(-10.38, 1636.71) * mm});
            skLineSegment(sketch, "E35.0.21.14", {"start": v(-19.9, 1639.89) * mm, "end": v(-19.9, 1636.71) * mm});
            skPoint(sketch, "E35.0.22.0", {"position": v(-15.14, 1733.55) * mm});
            skArc(sketch, "E35.0.22.1", {"start": v(-10.38, 1735.14) * mm, "mid": v(-15.14, 1739.9) * mm, "end": v(-19.9, 1735.14) * mm});
            skPoint(sketch, "E35.0.22.2", {"position": v(-15.14, 1714.5) * mm});
            skPoint(sketch, "E35.0.22.3", {"position": v(-15.14, 1695.45) * mm});
            skArc(sketch, "E35.0.22.4", {"start": v(-19.9, 1731.96) * mm, "mid": v(-15.14, 1727.2) * mm, "end": v(-10.38, 1731.96) * mm});
            skCircle(sketch, "E35.0.22.5", {"center": v(-15.14, 1695.45) * mm, "radius": 4.76 * mm});
            skCircle(sketch, "E35.0.22.6", {"center": v(-15.14, 1676.4) * mm, "radius": 4.76 * mm});
            skArc(sketch, "E35.0.22.7", {"start": v(-10.38, 1716.09) * mm, "mid": v(-15.14, 1720.85) * mm, "end": v(-19.9, 1716.09) * mm});
            skArc(sketch, "E35.0.22.8", {"start": v(-19.9, 1712.91) * mm, "mid": v(-15.14, 1708.15) * mm, "end": v(-10.38, 1712.91) * mm});
            skPoint(sketch, "E35.0.22.9", {"position": v(-15.14, 1733.55) * mm});
            skPoint(sketch, "E35.0.22.10", {"position": v(-15.14, 1714.5) * mm});
            skLineSegment(sketch, "E35.0.22.11", {"start": v(-19.9, 1735.14) * mm, "end": v(-19.9, 1731.96) * mm});
            skLineSegment(sketch, "E35.0.22.12", {"start": v(-10.38, 1735.14) * mm, "end": v(-10.38, 1731.96) * mm});
            skLineSegment(sketch, "E35.0.22.13", {"start": v(-10.38, 1716.09) * mm, "end": v(-10.38, 1712.91) * mm});
            skLineSegment(sketch, "E35.0.22.14", {"start": v(-19.9, 1716.09) * mm, "end": v(-19.9, 1712.91) * mm});
            skPoint(sketch, "E35.0.23.0", {"position": v(-15.14, 1809.75) * mm});
            skArc(sketch, "E35.0.23.1", {"start": v(-10.38, 1811.34) * mm, "mid": v(-15.14, 1816.1) * mm, "end": v(-19.9, 1811.34) * mm});
            skPoint(sketch, "E35.0.23.2", {"position": v(-15.14, 1790.7) * mm});
            skPoint(sketch, "E35.0.23.3", {"position": v(-15.14, 1771.65) * mm});
            skArc(sketch, "E35.0.23.4", {"start": v(-19.9, 1808.16) * mm, "mid": v(-15.14, 1803.4) * mm, "end": v(-10.38, 1808.16) * mm});
            skCircle(sketch, "E35.0.23.5", {"center": v(-15.14, 1771.65) * mm, "radius": 4.76 * mm});
            skCircle(sketch, "E35.0.23.6", {"center": v(-15.14, 1752.6) * mm, "radius": 4.76 * mm});
            skArc(sketch, "E35.0.23.7", {"start": v(-10.38, 1792.29) * mm, "mid": v(-15.14, 1797.05) * mm, "end": v(-19.9, 1792.29) * mm});
            skArc(sketch, "E35.0.23.8", {"start": v(-19.9, 1789.11) * mm, "mid": v(-15.14, 1784.35) * mm, "end": v(-10.38, 1789.11) * mm});
            skPoint(sketch, "E35.0.23.9", {"position": v(-15.14, 1809.75) * mm});
            skPoint(sketch, "E35.0.23.10", {"position": v(-15.14, 1790.7) * mm});
            skLineSegment(sketch, "E35.0.23.11", {"start": v(-19.9, 1811.34) * mm, "end": v(-19.9, 1808.16) * mm});
            skLineSegment(sketch, "E35.0.23.12", {"start": v(-10.38, 1811.34) * mm, "end": v(-10.38, 1808.16) * mm});
            skLineSegment(sketch, "E35.0.23.13", {"start": v(-10.38, 1792.29) * mm, "end": v(-10.38, 1789.11) * mm});
            skLineSegment(sketch, "E35.0.23.14", {"start": v(-19.9, 1792.29) * mm, "end": v(-19.9, 1789.11) * mm});
            skLineSegment(sketch, "E35.direction1", {"start": v(-15.14, 0) * mm, "end": v(10.99, 0) * mm, "construction": true});
            skLineSegment(sketch, "E35.direction2", {"start": v(-15.14, 0) * mm, "end": v(-15.14, 76.2) * mm, "construction": true});
            skSolve(sketch);
        }
        {
            var Q0;
            Q0=qSketchRegion(id+"F3",true);
            extrude(context, id + "F5", {"entities" : qUnion([Q0]), "operationType" : NewBodyOperationType.REMOVE, "endBound" : BoundingType.THROUGH_ALL, "oppositeDirection" : true, "depth" : 25.4 * mm, "offsetDistance" : 25.4 * mm});
        }
        {
            var Q0;
            Q0=qSketchRegion(id+"F4",true);
            extrude(context, id + "F6", {"entities" : qUnion([Q0]), "operationType" : NewBodyOperationType.REMOVE, "endBound" : BoundingType.THROUGH_ALL, "oppositeDirection" : true, "depth" : 25.4 * mm, "offsetDistance" : 25.4 * mm});
        }
        {
            var Q0;
            Q0=makeQuery(id+"F2.opExtrude","SWEPT_FACE",FACE,{"disambiguationData":[OSD([sQuery(id+"F1.wireOp",EDGE,"E1")])]});
            var sketch = newSketch(context, id + "F7", { "sketchPlane" : qUnion([Q0])});
            skLineSegment(sketch, "E36", {"start": v(1.37, 533.4) * mm, "end": v(-28.75, 533.4) * mm});
            skLineSegment(sketch, "E37", {"start": v(-28.75, 533.4) * mm, "end": v(-28.75, 503.28) * mm});
            skLineSegment(sketch, "E38", {"start": v(-28.75, 503.28) * mm, "end": v(1.37, 533.4) * mm});
            skLineSegment(sketch, "E39", {"start": v(-28.75, 0) * mm, "end": v(1.37, 0) * mm});
            skLineSegment(sketch, "E40", {"start": v(1.37, 0) * mm, "end": v(-28.75, 30.12) * mm});
            skLineSegment(sketch, "E41", {"start": v(-28.75, 30.12) * mm, "end": v(-28.75, 0) * mm});
            skSolve(sketch);
        }
        {
            var Q0;
            Q0 = qSketchRegion(id + "F7", true);
            extrude(context, id + "F8", {"entities" : qUnion([Q0]), "operationType" : NewBodyOperationType.REMOVE, "endBound" : BoundingType.THROUGH_ALL, "oppositeDirection" : true, "depth" : 25.4 * mm, "offsetDistance" : 25.4 * mm});
        }
    });
